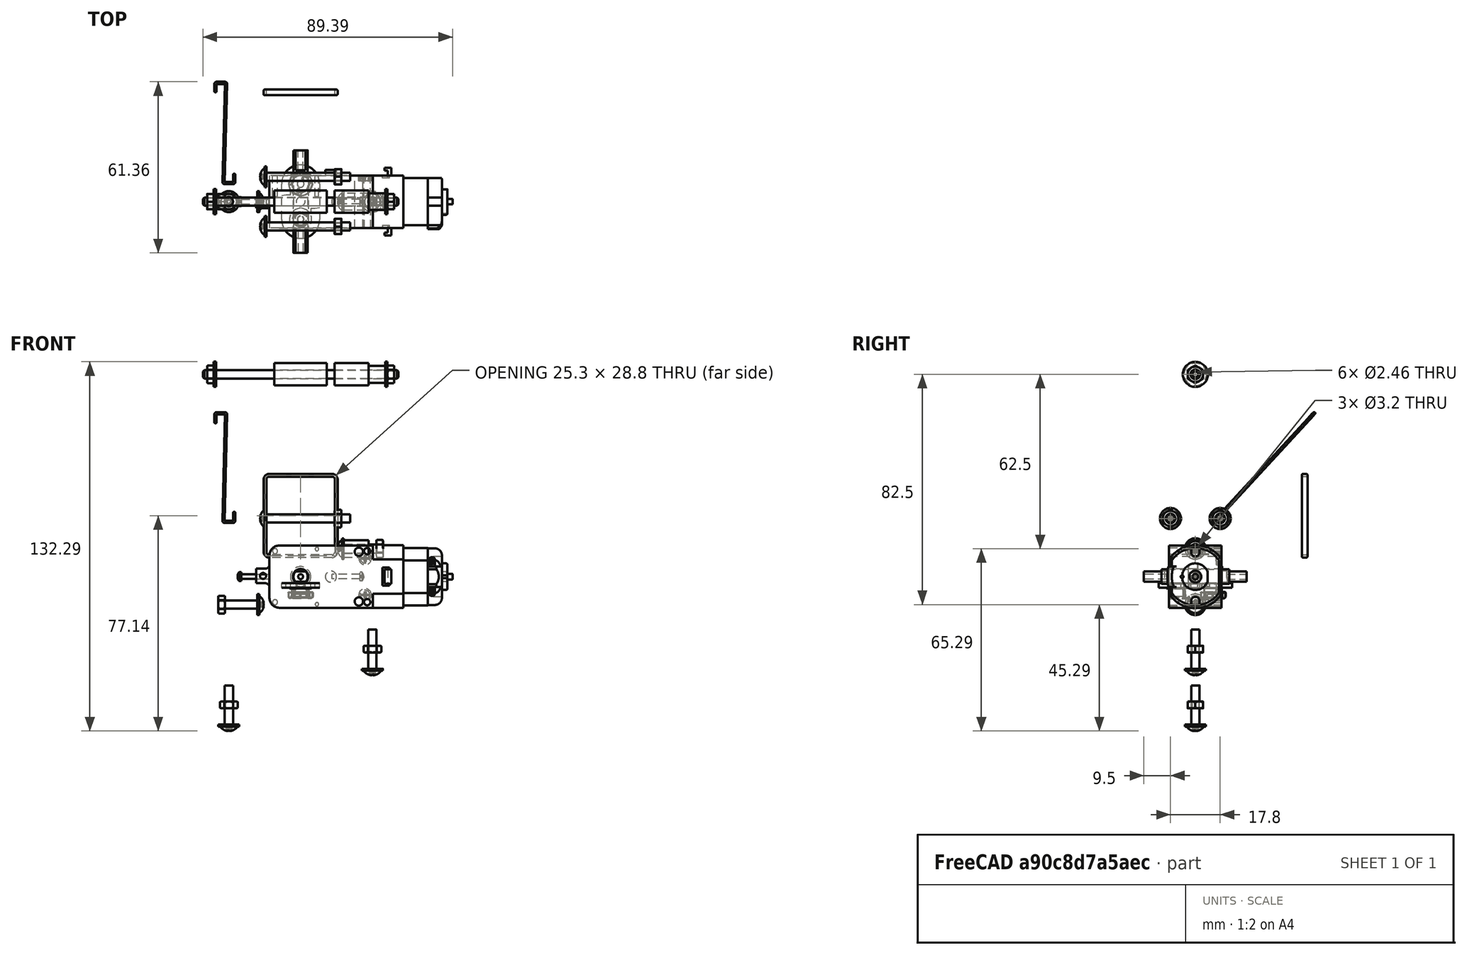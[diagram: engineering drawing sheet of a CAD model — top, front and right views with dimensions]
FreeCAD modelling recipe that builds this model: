
FCSTD DOCUMENT  (FreeCAD 0.21R33771 (Git))
Label: walking_robot_04
License: CERN Open Hardware Licence permissive
LicenseURL: https://cern-ohl.web.cern.ch/
objects: PartDesign::Body×27, PartDesign::SubShapeBinder×26, Sketcher::SketchObject×19, Part::FeaturePython×19, Part::Part2DObjectPython×19, PartDesign::Pad×15, PartDesign::FeatureBase×12, Part::Feature×10, PartDesign::Plane×7, App::DocumentObjectGroup×5, TechDraw::DrawViewDimension×5, PartDesign::FeaturePython×4, PartDesign::Fillet×3, Spreadsheet::Sheet×2, PartDesign::CoordinateSystem×2, Part::Box×2, Part::Cut×2, App::Part×2, PartDesign::AdditivePipe×1, TechDraw::DrawSVGTemplate×1, +4 more types
note: 194 computed .brp shape members not serialized (recipe doc carries the construction recipe); baked Part::Feature solids carry a one-line shape summary decoded from their .brp

FEATURE [Spreadsheet::Sheet] Spreadsheet
  cells = A1='acrylic_thick; B1(acrylic_thick)==4.9 mm; A2='acrylic_thin; B2(acrylic_thin)=2.8; A3='cam_length; B3(cam_length)=10; A4='angle; B4(angle)=270
FEATURE [Part::Feature] Compound002  label="motoreducteur001"
  Placement = pos=(25.85,-9.4,11.15) rot=(-1,0,0;1.5708rad)
  shape: bbox 70.34 x 38.2 x 22.5 mm, 234 faces, 3 solids (baked)
FEATURE [PartDesign::CoordinateSystem] Local_CS002
  AttacherType = Attacher::AttachEngine3D
  AttachmentOffset = pos=(0,0,0) rot=(0,-1,0;1.5708rad)
  MapMode = 11
  Placement = pos=(-2.8e-15,-19.1,1.8e-15) rot=(0,0,-1;1.5708rad)
  Support = -> [Compound002]
FEATURE [PartDesign::CoordinateSystem] Local_CS003
  AttacherType = Attacher::AttachEngine3D
  AttachmentOffset = pos=(0,0,0) rot=(0,1,0;1.5708rad)
  MapMode = 11
  Placement = pos=(-2.8e-15,19.1,1.9e-15) rot=(0,0,1;4.71239rad)
  Support = -> [Compound002]
FEATURE [PartDesign::SubShapeBinder] Binder
  BindCopyOnChange = 0
  BindMode = 0
  ClaimChildren = false
  Context = -> Body [Binder.]
  Fuse = false
  MakeFace = true
  OffsetFill = false
  OffsetIntersection = false
  OffsetJoinType = 0
  OffsetOpenResult = false
  PartialLoad = false
  Relative = true
  Support = -> [Part001]
  _Version = 2
FEATURE [Sketcher::SketchObject] Sketch
  ExternalGeometry = -> [Binder]
  FullyConstrained = true
  MapMode = 5
  Placement = pos=(-18.4,0,0) rot=(0.57735,-0.57735,-0.57735;2.0944rad)
  Support = -> [Binder]
  expr: Constraints[38] = Spreadsheet.cam_length
  expr: Constraints[81] = Spreadsheet.angle
  sketch-geometry (37):
    g0: ArcOfCircle CenterX=3.55 CenterY=5 CenterZ=0 NormalX=0 NormalY=0 NormalZ=1 AngleXU=0 Radius=0.4 StartAngle=0 EndAngle=3.14159
    g1: ArcOfCircle CenterX=3.55 CenterY=-5 CenterZ=0 NormalX=0 NormalY=0 NormalZ=1 AngleXU=0 Radius=0.4 StartAngle=3.14159 EndAngle=6.28319
    g2: LineSegment StartX=3.15 StartY=5 StartZ=0 EndX=3.15 EndY=-5 EndZ=0
    g3: LineSegment StartX=3.95 StartY=-5 StartZ=0 EndX=3.95 EndY=5 EndZ=0
    g4: ArcOfCircle CenterX=-3.55 CenterY=5 CenterZ=0 NormalX=0 NormalY=0 NormalZ=1 AngleXU=0 Radius=0.4 StartAngle=3e-16 EndAngle=3.14159
    g5: ArcOfCircle CenterX=-3.55 CenterY=-5 CenterZ=0 NormalX=0 NormalY=0 NormalZ=1 AngleXU=0 Radius=0.4 StartAngle=3.14159 EndAngle=6.28319
    g6: LineSegment StartX=-3.15 StartY=-5 StartZ=0 EndX=-3.15 EndY=5 EndZ=0
    g7: LineSegment StartX=3.55 StartY=5 StartZ=0 EndX=3.55 EndY=-5 EndZ=0
    g8: LineSegment StartX=-3.55 StartY=5 StartZ=0 EndX=-3.55 EndY=-5 EndZ=0
    g9: ArcOfCircle CenterX=1.55 CenterY=5 CenterZ=0 NormalX=0 NormalY=0 NormalZ=1 AngleXU=0 Radius=0.2 StartAngle=0 EndAngle=3.14159
    g10: ArcOfCircle CenterX=1.55 CenterY=-5 CenterZ=0 NormalX=0 NormalY=0 NormalZ=1 AngleXU=0 Radius=0.2 StartAngle=3.14159 EndAngle=6.28319
    g11: LineSegment StartX=1.35 StartY=5 StartZ=0 EndX=1.35 EndY=2.16333 EndZ=0
    g12: LineSegment StartX=1.75 StartY=-5 StartZ=0 EndX=1.75 EndY=5 EndZ=0
    g13: ArcOfCircle CenterX=-1.55 CenterY=5 CenterZ=0 NormalX=0 NormalY=0 NormalZ=1 AngleXU=0 Radius=0.2 StartAngle=5e-16 EndAngle=3.14159
    g14: ArcOfCircle CenterX=-1.55 CenterY=-5 CenterZ=0 NormalX=0 NormalY=0 NormalZ=1 AngleXU=0 Radius=0.2 StartAngle=3.14159 EndAngle=6.28319
    g15: LineSegment StartX=-1.75 StartY=5 StartZ=0 EndX=-1.75 EndY=-5 EndZ=0
    g16: LineSegment StartX=-1.35 StartY=-5 StartZ=0 EndX=-1.35 EndY=-2.16333 EndZ=0
    g17: LineSegment StartX=1.55 StartY=5 StartZ=0 EndX=1.55 EndY=-5 EndZ=0
    g18: LineSegment StartX=-1.55 StartY=5 StartZ=0 EndX=-1.55 EndY=-5 EndZ=0
    g19: LineSegment StartX=3.55 StartY=-4.2e-15 StartZ=0 EndX=1.55 EndY=-3.8e-15 EndZ=0
    g20: ArcOfCircle CenterX=9.6e-15 CenterY=5 CenterZ=0 NormalX=0 NormalY=0 NormalZ=1 AngleXU=0 Radius=7.5 StartAngle=0 EndAngle=3.14159
    g21: ArcOfCircle CenterX=6.9e-15 CenterY=-10 CenterZ=0 NormalX=0 NormalY=0 NormalZ=1 AngleXU=0 Radius=7.5 StartAngle=3.14159 EndAngle=6.28319
    g22: LineSegment StartX=-7.5 StartY=5 StartZ=0 EndX=-7.5 EndY=-10 EndZ=0
    g23: LineSegment StartX=7.5 StartY=-10 StartZ=0 EndX=7.5 EndY=5 EndZ=0
    g24: LineSegment StartX=8.7e-15 StartY=-3.6e-15 StartZ=0 EndX=9.6e-15 EndY=5 EndZ=0
    g25: LineSegment StartX=8.7e-15 StartY=-3.6e-15 StartZ=0 EndX=6.9e-15 EndY=-10 EndZ=0
    g26: Circle CenterX=6.9e-15 CenterY=-10 CenterZ=0 NormalX=0 NormalY=0 NormalZ=1 AngleXU=0 Radius=3.1
    g27: LineSegment StartX=-3.95 StartY=-5 StartZ=0 EndX=-3.95 EndY=5 EndZ=0
    g28: LineSegment StartX=1.55 StartY=-3.8e-15 StartZ=0 EndX=8.7e-15 EndY=-3.6e-15 EndZ=0
    g29: Circle CenterX=8.7e-15 CenterY=-3.6e-15 CenterZ=0 NormalX=0 NormalY=0 NormalZ=1 AngleXU=0 Radius=1.75
    g30: LineSegment StartX=-1.75 StartY=-4.1e-15 StartZ=0 EndX=-1.85 EndY=-4.1e-15 EndZ=0
    g31: LineSegment StartX=-3.55 StartY=-2.9e-15 StartZ=0 EndX=-1.55 EndY=-3.3e-15 EndZ=0
    g32: LineSegment StartX=8.7e-15 StartY=-3.6e-15 StartZ=0 EndX=-1.55 EndY=-3.3e-15 EndZ=0
    g33: LineSegment StartX=-1.35 StartY=2.16333 StartZ=0 EndX=-1.35 EndY=5 EndZ=0
    g34: LineSegment StartX=1.35 StartY=-2.16333 StartZ=0 EndX=1.35 EndY=-5 EndZ=0
    g35: ArcOfCircle CenterX=8.7e-15 CenterY=-3.6e-15 CenterZ=0 NormalX=0 NormalY=0 NormalZ=1 AngleXU=0 Radius=2.55 StartAngle=1.01289 EndAngle=2.1287
    g36: ArcOfCircle CenterX=8.7e-15 CenterY=-3.6e-15 CenterZ=0 NormalX=0 NormalY=0 NormalZ=1 AngleXU=0 Radius=2.55 StartAngle=4.15448 EndAngle=5.2703
  constraints (89):
    c: Tangent(g0,g2) = -1.5708
    c: Tangent(g2,g1) = -1.5708
    c: Tangent(g1,g3) = -1.5708
    c: Tangent(g5,g6) = -1.5708
    c: Tangent(g6,g4) = -1.5708
    c: Radius(g0) = 0.4
    c: Coincident(g7,g0)
    c: Coincident(g7,g1)
    c: Coincident(g8,g4)
    c: Coincident(g8,g5)
    c: Equal(g7,g8)
    c: Distance(g7) = 10
    c: Tangent(g9,g11) = -1.5708
    c: Tangent(g10,g12) = -1.5708
    c: Tangent(g12,g9) = -1.5708
    c: Tangent(g13,g15) = -1.5708
    c: Tangent(g15,g14) = -1.5708
    c: Tangent(g14,g16) = -1.5708
    c: Coincident(g17,g9)
    c: Coincident(g17,g10)
    c: Coincident(g18,g13)
    c: Coincident(g18,g14)
    c: Equal(g17,g7)
    c: Equal(g8,g18)
    c: Symmetric(g10,g9,g19)
    c: Distance(g19) = 2
    c: Perpendicular(g7,g19)
    c: Parallel(g17,g7)
    c: Parallel(g18,g8)
    c: Tangent(g20,g22) = -1.5708
    c: Tangent(g22,g21) = -1.5708
    c: Tangent(g21,g23) = -1.5708
    c: Tangent(g23,g20) = -1.5708
    c: Equal(g20,g21)
    c: Coincident(g24,g20)
    c: Coincident(g25,g21)
    c: Diameter(g20) = 15
    c: Distance(g24) = 5
    c: Distance(g25) = 10
    c: Coincident(g26,g21)
    c: Diameter(g26) = 6.2
    c: Tangent(g27,g4) = 1.5708
    c: Tangent(g27,g5) = 1.5708
    c: Symmetric(g0,g1,g19)
    c: Coincident(g28,g19)
    c: Parallel(g28,g19)
    c: Perpendicular(g28,g24)
    c: Tangent(g0,g3) = -1.5708
    c: PointOnObject(g30,g29)
    c: Horizontal(g30)
    c: Symmetric(g-5,g-5,g30)
    c: DistanceX(g30,g30) = 0.1
    c: Perpendicular(g25,g28)
    c: Symmetric(g14,g13,g31)
    c: Symmetric(g5,g4,g31)
    c: Equal(g31,g19)
    c: Coincident(g32,g31)
    c: Equal(g28,g32)
    c: Perpendicular(g32,g24)
    c: Perpendicular(g32,g18)
    c: Perpendicular(g18,g31)
    c: Tangent(g15,g29)
    c: PointOnObject(g34,g11)
    c: PointOnObject(g33,g-3)
    c: Parallel(g33,g17)
    c: Parallel(g17,g34)
    c: Tangent(g33,g13) = -1.5708
    c: Tangent(g34,g10) = -1.5708
    c: Coincident(g25,g32)
    c: Coincident(g25,g24)
    c: Coincident(g25,g28)
    c: Coincident(g24,g29)
    c: Coincident(g35,g24)
    c: Coincident(g35,g33)
    c: Coincident(g35,g11)
    c: Coincident(g36,g35)
    c: Coincident(g36,g34)
    c: Equal(g36,g-4)
    c: Coincident(g16,g36)
    c: Parallel(g16,g18)
    c: Coincident(g35,g-4)
    c: Angle(g25) = 4.71239
    c: Equal(g5,g1)
    c: Equal(g1,g4)
    c: Equal(g4,g0)
    c: Equal(g13,g9)
    c: Equal(g9,g14)
    c: Equal(g14,g10)
    c: Radius(g9) = 0.2
FEATURE [PartDesign::SubShapeBinder] Binder001
  BindCopyOnChange = 0
  BindMode = 0
  ClaimChildren = false
  Context = -> Body002 [Binder001.]
  Fuse = false
  MakeFace = true
  OffsetFill = false
  OffsetIntersection = false
  OffsetJoinType = 0
  OffsetOpenResult = false
  PartialLoad = false
  Relative = true
  Support = -> [Part001]
  _Version = 2
FEATURE [Part::Box] Box  label="Cube"
  AttacherType = Attacher::AttachEngine3D
  Height = 10
  Length = 10
  Placement = pos=(-5,18.4,-5) rot=(0,0,1;0rad)
  Width = 10
FEATURE [Part::Box] Box001  label="Cube001"
  AttacherType = Attacher::AttachEngine3D
  Height = 10
  Length = 10
  Placement = pos=(-5,-28.4,-5) rot=(0,0,1;0rad)
  Width = 10
FEATURE [Part::Cut] Cut
  Base = -> Compound002
  Tool = -> Box
FEATURE [Part::Cut] Cut001
  Base = -> Cut
  Tool = -> Box001
FEATURE [App::Part] Part001  label="Motor"
  Group = -> [Box001,Compound002,Local_CS002,Local_CS003,Box,Cut,Cut001]
  Origin = -> Origin004
  Placement = pos=(0,0,0) rot=(-0.57735,0.57735,-0.57735;4.18879rad)
FEATURE [PartDesign::Pad] Pad
  Direction = (-1,2e-16,-2e-16)
  Length = 2.8
  Length2 = 10
  Profile = -> Sketch
  ReferenceAxis = -> Sketch [N_Axis]
  Reversed = true
  Type = 0
  expr: Length = Spreadsheet.acrylic_thin
FEATURE [PartDesign::Body] Body  label="cam_right_1"
  Group = -> [Sketch,Binder,Pad]
  Origin = -> Origin001
  Tip = -> Pad
FEATURE [PartDesign::SubShapeBinder] Binder002
  BindCopyOnChange = 0
  BindMode = 0
  ClaimChildren = false
  Context = -> Body003 [Binder002.]
  Fuse = false
  MakeFace = true
  OffsetFill = false
  OffsetIntersection = false
  OffsetJoinType = 0
  OffsetOpenResult = false
  PartialLoad = false
  Relative = true
  Support = -> [Body]
  _Version = 2
FEATURE [PartDesign::Plane] DatumPlane001
  AttachmentOffset = pos=(0,0,0.1) rot=(0,0,1;0rad)
  Length = 60
  MapMode = 5
  Placement = pos=(-18.5,5.2e-15,-3.9e-15) rot=(-0.57735,0.57735,0.57735;4.18879rad)
  ResizeMode = 0
  Support = -> [Binder002]
  Width = 60
FEATURE [Sketcher::SketchObject] Sketch002
  ExternalGeometry = -> [Binder002]
  FullyConstrained = true
  MapMode = 5
  Placement = pos=(-18.5,5.2e-15,-3.9e-15) rot=(-0.57735,0.57735,0.57735;4.18879rad)
  Support = -> [DatumPlane001]
  sketch-geometry (6):
    g0: ArcOfCircle CenterX=-1.6948e-12 CenterY=5 CenterZ=0 NormalX=0 NormalY=0 NormalZ=1 AngleXU=0 Radius=7.5 StartAngle=2.58e-13 EndAngle=3.14159
    g1: ArcOfCircle CenterX=2.174e-12 CenterY=-10 CenterZ=0 NormalX=0 NormalY=0 NormalZ=1 AngleXU=0 Radius=7.5 StartAngle=3.14159 EndAngle=6.28319
    g2: LineSegment StartX=-7.5 StartY=5 StartZ=0 EndX=-7.5 EndY=-10 EndZ=0
    g3: LineSegment StartX=7.5 StartY=-10 StartZ=0 EndX=7.5 EndY=5 EndZ=0
    g4: Circle CenterX=2.174e-12 CenterY=-10 CenterZ=0 NormalX=0 NormalY=0 NormalZ=1 AngleXU=0 Radius=3.1
    g5: Circle CenterX=0 CenterY=0 CenterZ=0 NormalX=0 NormalY=0 NormalZ=1 AngleXU=0 Radius=1
  constraints (12):
    c: Tangent(g0,g2) = -1.5708
    c: Tangent(g2,g1) = -1.5708
    c: Tangent(g1,g3) = -1.5708
    c: Tangent(g3,g0) = -1.5708
    c: Equal(g0,g1)
    c: Coincident(g0,g-3)
    c: Coincident(g1,g-5)
    c: Equal(g0,g-3)
    c: Coincident(g4,g1)
    c: Equal(g4,g-5)
    c: Coincident(g5,g-6)
    c: Diameter(g5) = 2
FEATURE [PartDesign::Pad] Pad002
  Direction = (-1,2e-16,-2e-16)
  Length = 2.8
  Length2 = 10
  Placement = pos=(-18.5,5e-15,-4e-15) rot=(0.57735,-0.57735,-0.57735;2.0944rad)
  Profile = -> Sketch002
  ReferenceAxis = -> Sketch002 [N_Axis]
  Type = 0
  expr: Length = Spreadsheet.acrylic_thin
FEATURE [PartDesign::Body] Body003  label="cam_right_2"
  Group = -> [Binder002,DatumPlane001,Sketch002,Pad002]
  Origin = -> Origin
  Tip = -> Pad002
FEATURE [PartDesign::SubShapeBinder] Binder003
  BindCopyOnChange = 0
  BindMode = 0
  ClaimChildren = false
  Context = -> Body004 [Binder003.]
  Fuse = false
  MakeFace = true
  OffsetFill = false
  OffsetIntersection = false
  OffsetJoinType = 0
  OffsetOpenResult = false
  PartialLoad = false
  Relative = true
  Support = -> [Body003]
  _Version = 2
FEATURE [PartDesign::Plane] DatumPlane002
  AttachmentOffset = pos=(0,0,0.1) rot=(0,0,1;0rad)
  Length = 60
  MapMode = 5
  Placement = pos=(-21.4,5.3e-15,-1.05e-14) rot=(-0.57735,0.57735,0.57735;4.18879rad)
  ResizeMode = 0
  Support = -> [Binder003]
  Width = 60
FEATURE [Sketcher::SketchObject] Sketch003
  ExternalGeometry = -> [Binder003]
  FullyConstrained = true
  MapMode = 5
  Placement = pos=(-21.4,5.3e-15,-1.05e-14) rot=(-0.57735,0.57735,0.57735;4.18879rad)
  Support = -> [DatumPlane002]
  sketch-geometry (6):
    g0: ArcOfCircle CenterX=-1.6956e-12 CenterY=5 CenterZ=0 NormalX=0 NormalY=0 NormalZ=1 AngleXU=0 Radius=7.5 StartAngle=2.581e-13 EndAngle=3.14159
    g1: ArcOfCircle CenterX=2.1765e-12 CenterY=-10 CenterZ=0 NormalX=0 NormalY=0 NormalZ=1 AngleXU=0 Radius=7.5 StartAngle=3.14159 EndAngle=6.28319
    g2: LineSegment StartX=-7.5 StartY=5 StartZ=0 EndX=-7.5 EndY=-10 EndZ=0
    g3: LineSegment StartX=7.5 StartY=-10 StartZ=0 EndX=7.5 EndY=5 EndZ=0
    g4: Circle CenterX=2.1765e-12 CenterY=-10 CenterZ=0 NormalX=0 NormalY=0 NormalZ=1 AngleXU=0 Radius=3.1
    g5: Circle CenterX=0 CenterY=0 CenterZ=0 NormalX=0 NormalY=0 NormalZ=1 AngleXU=0 Radius=3
  constraints (12):
    c: Tangent(g0,g2) = -1.5708
    c: Tangent(g2,g1) = -1.5708
    c: Tangent(g1,g3) = -1.5708
    c: Tangent(g3,g0) = -1.5708
    c: Equal(g0,g1)
    c: Coincident(g0,g-3)
    c: Coincident(g1,g-5)
    c: Equal(g0,g-3)
    c: Coincident(g4,g1)
    c: Equal(g4,g-5)
    c: Coincident(g5,g-6)
    c: Diameter(g5) = 6
FEATURE [PartDesign::Pad] Pad003
  Direction = (-1,3e-16,-3e-16)
  Length = 2.8
  Length2 = 10
  Placement = pos=(-21.4,5e-15,-1e-14) rot=(0.57735,-0.57735,-0.57735;2.0944rad)
  Profile = -> Sketch003
  ReferenceAxis = -> Sketch003 [N_Axis]
  Type = 0
  expr: Length = Spreadsheet.acrylic_thin
FEATURE [PartDesign::Body] Body004  label="cam_right_3"
  Group = -> [Binder003,DatumPlane002,Sketch003,Pad003]
  Origin = -> Origin005
  Tip = -> Pad003
FEATURE [PartDesign::SubShapeBinder] Binder004
  BindCopyOnChange = 0
  BindMode = 0
  ClaimChildren = false
  Context = -> Body002 [Binder004.]
  Fuse = false
  MakeFace = true
  OffsetFill = false
  OffsetIntersection = false
  OffsetJoinType = 0
  OffsetOpenResult = false
  PartialLoad = false
  Relative = true
  Support = -> [Body004]
  _Version = 2
FEATURE [PartDesign::Plane] DatumPlane003
  AttachmentOffset = pos=(0,0,0.1) rot=(0,0,1;0rad)
  Length = 66.5529
  MapMode = 5
  Placement = pos=(-24.3,8.3e-15,-1.41e-14) rot=(-0.57735,0.57735,0.57735;4.18879rad)
  ResizeMode = 0
  Support = -> [Binder004]
  Width = 153.553
FEATURE [Sketcher::SketchObject] Sketch001
  ExternalGeometry = -> [Binder004]
  FullyConstrained = false
  MapMode = 5
  Placement = pos=(-24.3,8.3e-15,-1.41e-14) rot=(-0.57735,0.57735,0.57735;4.18879rad)
  Support = -> [DatumPlane003]
  expr: Constraints[92] = Spreadsheet.angle
  expr: Constraints[98] = Spreadsheet.acrylic_thin
  sketch-geometry (38):
    g0: LineSegment StartX=-10 StartY=84 StartZ=0 EndX=10 EndY=84 EndZ=0
    g1: LineSegment StartX=10 StartY=84 StartZ=0 EndX=10 EndY=-53 EndZ=0
    g2: LineSegment StartX=10 StartY=-53 StartZ=0 EndX=-10 EndY=-53 EndZ=0
    g3: LineSegment StartX=-10 StartY=-53 StartZ=0 EndX=-10 EndY=84 EndZ=0
    g4: LineSegment StartX=4e-15 StartY=-10 StartZ=0 EndX=-10 EndY=-10 EndZ=0
    g5: LineSegment StartX=4e-15 StartY=-10 StartZ=0 EndX=10 EndY=-10 EndZ=0
    g6: ArcOfCircle CenterX=-2e-16 CenterY=75 CenterZ=0 NormalX=0 NormalY=0 NormalZ=1 AngleXU=0 Radius=3.1 StartAngle=2e-16 EndAngle=3.14159
    g7: ArcOfCircle CenterX=6e-16 CenterY=50 CenterZ=0 NormalX=0 NormalY=0 NormalZ=1 AngleXU=0 Radius=3.1 StartAngle=3.14159 EndAngle=6.28319
    g8: LineSegment StartX=-3.1 StartY=75 StartZ=0 EndX=-3.1 EndY=50 EndZ=0
    g9: LineSegment StartX=3.1 StartY=50 StartZ=0 EndX=3.1 EndY=75 EndZ=0
    g10: LineSegment StartX=-2e-16 StartY=75 StartZ=0 EndX=-4e-16 EndY=84 EndZ=0
    g11: Circle CenterX=4e-15 CenterY=-10 CenterZ=0 NormalX=0 NormalY=0 NormalZ=1 AngleXU=0 Radius=1.55
    g12: LineSegment StartX=0 StartY=0 StartZ=0 EndX=4e-15 EndY=-10 EndZ=0
    g13: Circle CenterX=0 CenterY=71 CenterZ=0 NormalX=0 NormalY=0 NormalZ=1 AngleXU=0 Radius=3.1
    g14: LineSegment StartX=0 StartY=71 StartZ=0 EndX=0 EndY=0 EndZ=0
    g15: LineSegment StartX=6e-16 StartY=50 StartZ=0 EndX=1e-16 EndY=62.5 EndZ=0
    g16: LineSegment StartX=-2e-16 StartY=75 StartZ=0 EndX=1e-16 EndY=62.5 EndZ=0
    g17: LineSegment StartX=-10 StartY=-53 StartZ=0 EndX=-6 EndY=-53 EndZ=0
    g18: LineSegment StartX=-6 StartY=-53 StartZ=0 EndX=-6 EndY=-50.2 EndZ=0
    g19: LineSegment StartX=-6 StartY=-50.2 StartZ=0 EndX=-1.25 EndY=-50.2 EndZ=0
    g20: LineSegment StartX=-1.25 StartY=-50.2 StartZ=0 EndX=-1.25 EndY=-47.2 EndZ=0
    g21: LineSegment StartX=-1.25 StartY=-47.2 StartZ=0 EndX=-2.75 EndY=-47.2 EndZ=0
    g22: LineSegment StartX=-2.75 StartY=-47.2 StartZ=0 EndX=-2.75 EndY=-44.7 EndZ=0
    g23: LineSegment StartX=-2.75 StartY=-44.7 StartZ=0 EndX=-1.25 EndY=-44.7 EndZ=0
    g24: LineSegment StartX=-1.25 StartY=-44.7 StartZ=0 EndX=-1.25 EndY=-37.7 EndZ=0
    g25: LineSegment StartX=-1.25 StartY=-37.7 StartZ=0 EndX=1.25 EndY=-37.7 EndZ=0
    g26: LineSegment StartX=1.25 StartY=-37.7 StartZ=0 EndX=1.25 EndY=-44.7 EndZ=0
    g27: LineSegment StartX=1.25 StartY=-44.7 StartZ=0 EndX=2.75 EndY=-44.7 EndZ=0
    g28: LineSegment StartX=2.75 StartY=-44.7 StartZ=0 EndX=2.75 EndY=-47.2 EndZ=0
    g29: LineSegment StartX=2.75 StartY=-47.2 StartZ=0 EndX=1.25 EndY=-47.2 EndZ=0
    g30: LineSegment StartX=1.25 StartY=-47.2 StartZ=0 EndX=1.25 EndY=-50.2 EndZ=0
    g31: LineSegment StartX=1.25 StartY=-50.2 StartZ=0 EndX=6 EndY=-50.2 EndZ=0
    g32: LineSegment StartX=6 StartY=-50.2 StartZ=0 EndX=6 EndY=-53 EndZ=0
    g33: LineSegment StartX=6 StartY=-53 StartZ=0 EndX=10 EndY=-53 EndZ=0
    g34: LineSegment StartX=-7 StartY=-10 StartZ=0 EndX=-7 EndY=20 EndZ=0
    g35: LineSegment StartX=7 StartY=20 StartZ=0 EndX=7 EndY=-10 EndZ=0
    g36: Circle CenterX=-7 CenterY=20 CenterZ=0 NormalX=0 NormalY=0 NormalZ=1 AngleXU=0 Radius=0.6
    g37: Circle CenterX=7 CenterY=20 CenterZ=0 NormalX=0 NormalY=0 NormalZ=1 AngleXU=0 Radius=0.6
  constraints (105):
    c: Coincident(g0,g1)
    c: Coincident(g1,g2)
    c: Coincident(g2,g3)
    c: Coincident(g3,g0)
    c: Distance(g0) = 20
    c: Perpendicular(g3,g0)
    c: Perpendicular(g1,g2)
    c: Perpendicular(g2,g3)
    c: PointOnObject(g4,g3)
    c: PointOnObject(g5,g1)
    c: Perpendicular(g1,g5)
    c: Perpendicular(g3,g4)
    c: Equal(g4,g5)
    c: Distance(g3) = 137
    c: Tangent(g6,g8) = -1.5708
    c: Tangent(g8,g7) = -1.5708
    c: Tangent(g7,g9) = -1.5708
    c: Tangent(g9,g6) = -1.5708
    c: Equal(g6,g7)
    c: Diameter(g7) = 6.2
    c: Distance(g6,g7) = 25
    c: Coincident(g10,g6)
    c: Perpendicular(g0,g10)
    c: Distance(g10) = 9
    c: Symmetric(g0,g0,g10)
    c: Parallel(g8,g3)
    c: Diameter(g11) = 3.1
    c: Coincident(g14,g13)
    c: DistanceY(g14,g14) = 71
    c: Coincident(g14,g12)
    c: Coincident(g15,g7)
    c: Coincident(g16,g6)
    c: Coincident(g16,g15)
    c: Equal(g16,g15)
    c: Parallel(g16,g8)
    c: Tangent(g13,g9)
    c: Vertical(g14)
    c: Coincident(g17,g3)
    c: Coincident(g17,g18)
    c: Coincident(g18,g19)
    c: Coincident(g19,g20)
    c: Coincident(g20,g21)
    c: Coincident(g21,g22)
    c: Coincident(g22,g23)
    c: Coincident(g23,g24)
    c: Coincident(g24,g25)
    c: Coincident(g25,g26)
    c: Coincident(g26,g27)
    c: Coincident(g27,g28)
    c: Coincident(g28,g29)
    c: Coincident(g29,g30)
    c: Coincident(g30,g31)
    c: Coincident(g31,g32)
    c: Coincident(g32,g33)
    c: Coincident(g33,g1)
    c: Perpendicular(g17,g3)
    c: Perpendicular(g33,g1)
    c: Perpendicular(g32,g33)
    c: Perpendicular(g17,g18)
    c: Perpendicular(g19,g18)
    c: Perpendicular(g32,g31)
    c: Perpendicular(g31,g30)
    c: Perpendicular(g19,g20)
    c: Perpendicular(g29,g30)
    c: Perpendicular(g20,g21)
    c: Perpendicular(g28,g29)
    c: Perpendicular(g22,g21)
    c: Perpendicular(g28,g27)
    c: Perpendicular(g23,g22)
    c: Perpendicular(g27,g26)
    c: Perpendicular(g24,g23)
    c: Equal(g18,g32)
    c: Equal(g30,g20)
    c: Equal(g29,g21)
    c: Equal(g23,g27)
    c: Equal(g19,g31)
    c: Distance(g22,g27) = 5.5
    c: Equal(g25,g22)
    c: Equal(g22,g28)
    c: Distance(g24) = 7
    c: Perpendicular(g25,g26)
    c: Equal(g21,g23)
    c: PointOnObject(g34,g4)
    c: Equal(g34,g35)
    c: Distance(g34,g4) = 3
    c: Coincident(g36,g34)
    c: Coincident(g37,g35)
    c: Equal(g37,g36)
    c: Diameter(g37) = 1.2
    c: Distance(g34) = 30
    c: Perpendicular(g5,g35)
    c: Perpendicular(g4,g34)
    c: Angle(g12) = 4.71239
    c: Equal(g17,g33)
    c: Distance(g17) = 4
    c: DistanceY(g3,g12) = 53
    c: Coincident(g12,g-1)
    c: DistanceY(g22,g22) = 2.5
    c: DistanceY(g18,g18) = 2.8
    c: DistanceY(g20,g20) = 3
    c: Equal(g7,g13)
    c: Coincident(g4,g5)
    c: Coincident(g4,g12)
    c: Coincident(g4,g-3)
    c: Coincident(g4,g11)
FEATURE [PartDesign::Pad] Pad004
  Direction = (-1,5e-16,-5e-16)
  Length = 2.8
  Length2 = 10
  Placement = pos=(-24.3,8e-15,-1.4e-14) rot=(0.57735,-0.57735,-0.57735;2.0944rad)
  Profile = -> Sketch001
  ReferenceAxis = -> Sketch001 [N_Axis]
  Type = 0
  expr: Length = Spreadsheet.acrylic_thin
FEATURE [PartDesign::SubShapeBinder] Binder005
  BindCopyOnChange = 0
  BindMode = 0
  ClaimChildren = false
  Context = -> Body005 [Binder005.]
  Fuse = false
  MakeFace = true
  OffsetFill = false
  OffsetIntersection = false
  OffsetJoinType = 0
  OffsetOpenResult = false
  PartialLoad = false
  Relative = true
  Support = -> [Body004]
  _Version = 2
FEATURE [Part::FeaturePython] Screw  label="M3x14-Screw"  # Fasteners workbench fastener (typed FeaturePython)
  Placement = pos=(-15.5,7.6099e-12,-10) rot=(0,1,0;1.5708rad)
  diameter = 1
  invert = false
  leftHanded = false
  length = 6
  lengthCustom = 14
  matchOuter = false
  offset = 0
  thread = false
  type = 25
FEATURE [Part::FeaturePython] Nut  label="M3-Nut"  # Fasteners workbench fastener (typed FeaturePython)
  Placement = pos=(-29.5,7.6239e-12,-10) rot=(0,1,0;1.5708rad)
  baseObject = -> Screw [Edge71]
  diameter = 4
  invert = false
  leftHanded = false
  matchOuter = false
  offset = 0
  thread = false
  type = 25
FEATURE [PartDesign::SubShapeBinder] Binder008
  BindCopyOnChange = 0
  BindMode = 0
  ClaimChildren = false
  Context = -> Body005 [Binder008.]
  Fuse = false
  MakeFace = true
  OffsetFill = false
  OffsetIntersection = false
  OffsetJoinType = 0
  OffsetOpenResult = false
  PartialLoad = false
  Relative = true
  Support = -> [Body002[Pad004.]]
  _Version = 2
FEATURE [Sketcher::SketchObject] Sketch004
  ExternalGeometry = -> [Binder005]
  FullyConstrained = true
  MapMode = 5
  Placement = pos=(-24.3,-1.36e-14,-3.65e-14) rot=(0.57735,0.57735,0.57735;2.0944rad)
  Support = -> [Binder008]
  sketch-geometry (2):
    g0: Circle CenterX=-2.172e-12 CenterY=-10 CenterZ=0 NormalX=0 NormalY=0 NormalZ=1 AngleXU=0 Radius=3
    g1: Circle CenterX=-2.172e-12 CenterY=-10 CenterZ=0 NormalX=0 NormalY=0 NormalZ=1 AngleXU=0 Radius=1.6
  constraints (4):
    c: Diameter(g1) = 3.2
    c: Diameter(g0) = 6
    c: Coincident(g1,g-3)
    c: Coincident(g0,g1)
FEATURE [PartDesign::Pad] Pad005
  Direction = (1,0,4e-16)
  Length = 8.8
  Length2 = 10
  Profile = -> Sketch004
  ReferenceAxis = -> Sketch004 [N_Axis]
  Type = 0
FEATURE [PartDesign::Body] Body005  label="spacer_right"
  Group = -> [Binder005,Sketch004,Pad005,Binder008]
  Origin = -> Origin006
  Tip = -> Pad005
FEATURE [PartDesign::SubShapeBinder] Binder009
  BindCopyOnChange = 0
  BindMode = 0
  ClaimChildren = false
  Context = -> Body007 [Binder009.]
  Fuse = false
  MakeFace = true
  OffsetFill = false
  OffsetIntersection = false
  OffsetJoinType = 0
  OffsetOpenResult = false
  PartialLoad = false
  Relative = true
  Support = -> [Body002[Pad004.]]
  _Version = 2
FEATURE [PartDesign::Plane] DatumPlane
  Length = 74.3266
  MapMode = 5
  Placement = pos=(5.3e-14,-1.145e-13,-53) rot=(1,0,0;3.14159rad)
  ResizeMode = 0
  Support = -> [Binder009]
  Width = 119.627
FEATURE [Sketcher::SketchObject] Sketch006
  ExternalGeometry = -> [Binder009]
  FullyConstrained = true
  MapMode = 5
  Placement = pos=(5.3e-14,-1.145e-13,-53) rot=(0,0,1;3.14159rad)
  Support = -> [DatumPlane]
  sketch-geometry (51):
    g0: LineSegment StartX=-12.3 StartY=40 StartZ=0 EndX=25.7 EndY=40 EndZ=0
    g1: LineSegment StartX=25.7 StartY=40 StartZ=0 EndX=25.7 EndY=0 EndZ=0
    g2: LineSegment StartX=25.7 StartY=0 StartZ=0 EndX=25.7 EndY=-56 EndZ=0
    g3: LineSegment StartX=25.7 StartY=-56 StartZ=0 EndX=-12.3 EndY=-56 EndZ=0
    g4: ArcOfCircle CenterX=-12.3 CenterY=40 CenterZ=0 NormalX=0 NormalY=0 NormalZ=1 AngleXU=0 Radius=4 StartAngle=1.5708 EndAngle=4.71239
    g5: ArcOfCircle CenterX=-12.3 CenterY=-56 CenterZ=0 NormalX=0 NormalY=0 NormalZ=1 AngleXU=0 Radius=4 StartAngle=1.5708 EndAngle=4.71239
    g6: LineSegment StartX=-12.3 StartY=44 StartZ=0 EndX=25.7 EndY=44 EndZ=0
    g7: LineSegment StartX=-12.3 StartY=36 StartZ=0 EndX=15.7 EndY=36 EndZ=0
    g8: LineSegment StartX=-12.3 StartY=-52 StartZ=0 EndX=15.7 EndY=-52 EndZ=0
    g9: LineSegment StartX=-12.3 StartY=-60 StartZ=0 EndX=25.7 EndY=-60 EndZ=0
    g10: ArcOfCircle CenterX=25.7 CenterY=10.1 CenterZ=0 NormalX=0 NormalY=0 NormalZ=1 AngleXU=0 Radius=8 StartAngle=0 EndAngle=0.895665
    g11: ArcOfCircle CenterX=25.7 CenterY=-9.9 CenterZ=0 NormalX=0 NormalY=0 NormalZ=1 AngleXU=0 Radius=8 StartAngle=3.14159 EndAngle=4.03726
    g12: LineSegment StartX=17.7 StartY=10.1 StartZ=0 EndX=17.7 EndY=-9.9 EndZ=0
    g13: LineSegment StartX=33.7 StartY=-9.9 StartZ=0 EndX=33.7 EndY=10.1 EndZ=0
    g14: LineSegment StartX=20.7 StartY=31 StartZ=0 EndX=20.7 EndY=16.345 EndZ=0
    g15: LineSegment StartX=30.7 StartY=16.345 StartZ=0 EndX=30.7 EndY=39 EndZ=0
    g16: ArcOfCircle CenterX=25.7 CenterY=39 CenterZ=0 NormalX=0 NormalY=0 NormalZ=1 AngleXU=0 Radius=5 StartAngle=0 EndAngle=1.5708
    g17: LineSegment StartX=20.7 StartY=-47 StartZ=0 EndX=20.7 EndY=-16.145 EndZ=0
    g18: LineSegment StartX=30.7 StartY=-16.145 StartZ=0 EndX=30.7 EndY=-55 EndZ=0
    g19: ArcOfCircle CenterX=25.7 CenterY=-55 CenterZ=0 NormalX=0 NormalY=0 NormalZ=1 AngleXU=0 Radius=5 StartAngle=4.71239 EndAngle=6.28319
    g20: ArcOfCircle CenterX=25.7 CenterY=-9.9 CenterZ=0 NormalX=0 NormalY=0 NormalZ=1 AngleXU=0 Radius=8 StartAngle=5.38752 EndAngle=6.28319
    g21: ArcOfCircle CenterX=25.7 CenterY=10.1 CenterZ=0 NormalX=0 NormalY=0 NormalZ=1 AngleXU=0 Radius=8 StartAngle=2.24593 EndAngle=3.14159
    g22: Circle CenterX=25.7 CenterY=0 CenterZ=0 NormalX=0 NormalY=0 NormalZ=1 AngleXU=0 Radius=1.55
    g23: LineSegment StartX=24.2 StartY=10.1 StartZ=0 EndX=27.2 EndY=10.1 EndZ=0
    g24: LineSegment StartX=27.2 StartY=10.1 StartZ=0 EndX=27.2 EndY=6.1 EndZ=0
    g25: LineSegment StartX=27.2 StartY=6.1 StartZ=0 EndX=24.2 EndY=6.1 EndZ=0
    g26: LineSegment StartX=24.2 StartY=6.1 StartZ=0 EndX=24.2 EndY=10.1 EndZ=0
    g27: LineSegment StartX=24.3 StartY=10 StartZ=0 EndX=24.3 EndY=10.1 EndZ=0
    g28: LineSegment StartX=24.3 StartY=10 StartZ=0 EndX=24.2 EndY=10 EndZ=0
    g29: LineSegment StartX=27.1 StartY=6 StartZ=0 EndX=27.2 EndY=6 EndZ=0
    g30: LineSegment StartX=27.1 StartY=6 StartZ=0 EndX=27.1 EndY=6.1 EndZ=0
    g31: LineSegment StartX=24.2 StartY=-5.9 StartZ=0 EndX=27.2 EndY=-5.9 EndZ=0
    g32: LineSegment StartX=27.2 StartY=-5.9 StartZ=0 EndX=27.2 EndY=-9.9 EndZ=0
    g33: LineSegment StartX=27.2 StartY=-9.9 StartZ=0 EndX=24.2 EndY=-9.9 EndZ=0
    g34: LineSegment StartX=24.2 StartY=-9.9 StartZ=0 EndX=24.2 EndY=-5.9 EndZ=0
    g35: LineSegment StartX=24.3 StartY=-6 StartZ=0 EndX=24.3 EndY=-5.9 EndZ=0
    g36: LineSegment StartX=24.3 StartY=-6 StartZ=0 EndX=24.2 EndY=-6 EndZ=0
    g37: LineSegment StartX=27.1 StartY=-10 StartZ=0 EndX=27.2 EndY=-10 EndZ=0
    g38: LineSegment StartX=27.1 StartY=-10 StartZ=0 EndX=27.1 EndY=-9.9 EndZ=0
    g39: ArcOfCircle CenterX=15.7 CenterY=-47 CenterZ=0 NormalX=0 NormalY=0 NormalZ=1 AngleXU=0 Radius=5 StartAngle=4.71239 EndAngle=6.28319
    g40: GeomPoint X=20.7 Y=-52 Z=0
    g41: ArcOfCircle CenterX=15.7 CenterY=31 CenterZ=0 NormalX=0 NormalY=0 NormalZ=1 AngleXU=0 Radius=5 StartAngle=0 EndAngle=1.5708
    g42: GeomPoint X=20.7 Y=36 Z=0
    g43: LineSegment StartX=24.2 StartY=10.1 StartZ=0 EndX=17.7 EndY=10.1 EndZ=0
    g44: LineSegment StartX=27.2 StartY=10.1 StartZ=0 EndX=33.7 EndY=10.1 EndZ=0
    g45: LineSegment StartX=24.2 StartY=-9.9 StartZ=0 EndX=17.7 EndY=-9.9 EndZ=0
    g46: LineSegment StartX=27.2 StartY=-9.9 StartZ=0 EndX=33.7 EndY=-9.9 EndZ=0
    g47: LineSegment StartX=24.3 StartY=1.25 StartZ=0 EndX=24.3 EndY=-1.25 EndZ=0
    g48: LineSegment StartX=27.1 StartY=1.25 StartZ=0 EndX=27.1 EndY=-1.25 EndZ=0
    g49: LineSegment StartX=24.3 StartY=1e-15 StartZ=0 EndX=25.7 EndY=0 EndZ=0
    g50: LineSegment StartX=25.7 StartY=0 StartZ=0 EndX=27.1 EndY=1e-15 EndZ=0
  constraints (133):
    c: Horizontal(g0)
    c: Coincident(g0,g1)
    c: Vertical(g1)
    c: Coincident(g1,g2)
    c: Vertical(g2)
    c: Coincident(g2,g3)
    c: Horizontal(g3)
    c: DistanceY(g2,g2) = 56
    c: Equal(g3,g0)
    c: DistanceX(g0,g0) = 38
    c: Coincident(g4,g0)
    c: Coincident(g5,g3)
    c: Equal(g5,g4)
    c: Diameter(g5) = 8
    c: Horizontal(g6)
    c: Horizontal(g7)
    c: Tangent(g4,g6) = 1.5708
    c: Tangent(g4,g7) = -1.5708
    c: Distance(g42,g1) = 5
    c: Horizontal(g8)
    c: Horizontal(g9)
    c: Tangent(g5,g8) = 1.5708
    c: Tangent(g5,g9) = -1.5708
    c: Equal(g6,g9)
    c: Tangent(g12,g11) = -1.5708
    c: Tangent(g13,g10) = -1.5708
    c: Equal(g10,g11)
    c: Diameter(g10) = 16
    c: Vertical(g14)
    c: PointOnObject(g6,g1)
    c: Vertical(g15)
    c: Tangent(g15,g16) = -1.5708
    c: Tangent(g16,g6) = 1.5708
    c: Distance(g15,g1) = 5
    c: Vertical(g17)
    c: Vertical(g18)
    c: Distance(g18,g2) = 5
    c: Tangent(g19,g9) = -1.5708
    c: Tangent(g19,g18) = 1.5708
    c: Equal(g11,g20)
    c: Coincident(g11,g17)
    c: Coincident(g20,g18)
    c: Coincident(g11,g20)
    c: Tangent(g20,g13) = -1.5708
    c: Equal(g10,g21)
    c: Coincident(g21,g14)
    c: Coincident(g10,g21)
    c: Coincident(g10,g15)
    c: Tangent(g21,g12) = -1.5708
    c: Coincident(g22,g1)
    c: Diameter(g22) = 3.1
    c: Coincident(g23,g24)
    c: Coincident(g24,g25)
    c: Coincident(g25,g26)
    c: Coincident(g26,g23)
    c: Coincident(g28,g27)
    c: Coincident(g30,g29)
    c: Equal(g28,g27)
    c: Equal(g27,g30)
    c: Equal(g30,g29)
    c: Coincident(g31,g32)
    c: Coincident(g32,g33)
    c: Coincident(g33,g34)
    c: Coincident(g34,g31)
    c: Coincident(g36,g35)
    c: Coincident(g38,g37)
    c: Coincident(g37,g-5)
    c: Coincident(g35,g-6)
    c: Coincident(g-4,g29)
    c: Coincident(g27,g-3)
    c: PointOnObject(g40,g8)
    c: PointOnObject(g40,g17)
    c: Tangent(g8,g39) = -1.5708
    c: Tangent(g17,g39) = -1.5708
    c: Radius(g39) = 5
    c: Symmetric(g11,g18,g2)
    c: PointOnObject(g42,g7)
    c: PointOnObject(g42,g14)
    c: Tangent(g7,g41) = 1.5708
    c: Tangent(g14,g41) = 1.5708
    c: Equal(g41,g39)
    c: DistanceY(g1,g1) = 40
    c: Distance(g27) = 0.1
    c: Perpendicular(g-3,g27)
    c: Perpendicular(g28,g27)
    c: PointOnObject(g28,g26)
    c: PointOnObject(g27,g23)
    c: Perpendicular(g28,g26)
    c: Perpendicular(g23,g27)
    c: Perpendicular(g-4,g30)
    c: Perpendicular(g29,g30)
    c: PointOnObject(g29,g24)
    c: PointOnObject(g30,g25)
    c: Perpendicular(g25,g30)
    c: Perpendicular(g29,g24)
    c: Perpendicular(g-5,g38)
    c: Perpendicular(g37,g38)
    c: Perpendicular(g35,g-6)
    c: Perpendicular(g36,g35)
    c: Equal(g35,g36)
    c: Equal(g36,g37)
    c: Equal(g37,g38)
    c: Equal(g38,g27)
    c: PointOnObject(g35,g31)
    c: PointOnObject(g36,g34)
    c: Perpendicular(g34,g36)
    c: Perpendicular(g31,g35)
    c: PointOnObject(g38,g33)
    c: PointOnObject(g37,g32)
    c: Perpendicular(g32,g37)
    c: Perpendicular(g33,g38)
    c: Coincident(g43,g23)
    c: Coincident(g43,g12)
    c: Coincident(g44,g23)
    c: Coincident(g44,g10)
    c: Perpendicular(g44,g24)
    c: Perpendicular(g43,g26)
    c: Coincident(g45,g33)
    c: Coincident(g45,g11)
    c: Coincident(g46,g32)
    c: Coincident(g46,g13)
    c: Perpendicular(g32,g46)
    c: Coincident(g47,g-8)
    c: Coincident(g47,g-7)
    c: Coincident(g48,g-8)
    c: Coincident(g48,g-7)
    c: Coincident(g50,g49)
    c: PointOnObject(g50,g48)
    c: Equal(g49,g50)
    c: Perpendicular(g49,g47)
    c: Perpendicular(g48,g50)
    c: Symmetric(g47,g47,g49)
    c: Coincident(g22,g49)
FEATURE [PartDesign::Pad] Pad006
  Direction = (-6e-16,2.1e-15,1)
  Length = 2.8
  Length2 = 10
  Placement = pos=(2.9e-14,-1.09e-13,-53) rot=(1,0,0;3.14159rad)
  Profile = -> Sketch006
  ReferenceAxis = -> Sketch006 [N_Axis]
  Type = 0
  expr: Length = Spreadsheet.acrylic_thin
FEATURE [PartDesign::Body] Body007  label="feet_right"
  Group = -> [Sketch006,Binder009,DatumPlane,Pad006]
  Origin = -> Origin009
  Tip = -> Pad006
FEATURE [PartDesign::FeatureBase] Clone
  BaseFeature = -> Body
FEATURE [PartDesign::Body] Body008  label="cam_left_1"
  Group = -> [Clone]
  Origin = -> Origin010
  Placement = pos=(0,0,0) rot=(0,1,0;3.14159rad)
  Tip = -> Clone
FEATURE [PartDesign::FeatureBase] Clone001
  BaseFeature = -> Body003
FEATURE [PartDesign::Body] Body009  label="cam_left_2"
  Group = -> [Clone001]
  Origin = -> Origin011
  Placement = pos=(0,0,0) rot=(0,1,0;3.14159rad)
  Tip = -> Clone001
FEATURE [PartDesign::FeatureBase] Clone002
  BaseFeature = -> Body004
FEATURE [PartDesign::Body] Body010  label="cam_left_3"
  Group = -> [Clone002]
  Origin = -> Origin012
  Placement = pos=(0,0,0) rot=(0,1,0;3.14159rad)
  Tip = -> Clone002
FEATURE [PartDesign::FeatureBase] Clone003
  BaseFeature = -> Body005
FEATURE [PartDesign::Body] Body011  label="spacer_left"
  Group = -> [Clone003]
  Origin = -> Origin013
  Placement = pos=(0,0,0) rot=(0,1,0;3.14159rad)
  Tip = -> Clone003
FEATURE [PartDesign::FeatureBase] Clone007
  BaseFeature = -> Body007
FEATURE [PartDesign::Body] Body015  label="feet_left"
  Group = -> [Clone007]
  Origin = -> Origin017
  Placement = pos=(1e-14,0,-83.2) rot=(0,1,0;3.14159rad)
  Tip = -> Clone007
FEATURE [PartDesign::Fillet] Fillet
  Base = -> Pad004 [Edge1,Edge2,Edge11,Edge14,Edge53,Edge20,Edge38,Edge35,Edge50,Edge23,Edge41,Edge32,Edge26,Edge47,Edge44,Edge29]
  BaseFeature = -> Pad004
  Placement = pos=(-24.3,8e-15,-1.4e-14) rot=(0.57735,-0.57735,-0.57735;2.0944rad)
  Radius = 0.4
  SupportTransform = false
  UseAllEdges = false
FEATURE [PartDesign::Fillet] Fillet001
  Base = -> Fillet [Edge91,Edge93]
  BaseFeature = -> Fillet
  Placement = pos=(-24.3,8e-15,-1.4e-14) rot=(0.57735,-0.57735,-0.57735;2.0944rad)
  Radius = 5
  SupportTransform = false
  UseAllEdges = false
FEATURE [PartDesign::SubShapeBinder] Binder010
  BindCopyOnChange = 0
  BindMode = 0
  ClaimChildren = false
  Context = -> Body017 [Binder010.]
  Fuse = false
  MakeFace = true
  OffsetFill = false
  OffsetIntersection = false
  OffsetJoinType = 0
  OffsetOpenResult = false
  PartialLoad = false
  Relative = true
  Support = -> [Part001]
  _Version = 2
FEATURE [PartDesign::SubShapeBinder] Binder011
  BindCopyOnChange = 0
  BindMode = 0
  ClaimChildren = false
  Context = -> Body017 [Binder011.]
  Fuse = false
  MakeFace = true
  OffsetFill = false
  OffsetIntersection = false
  OffsetJoinType = 0
  OffsetOpenResult = false
  PartialLoad = false
  Relative = true
  Support = -> [Body002]
  _Version = 2
FEATURE [PartDesign::SubShapeBinder] Binder012
  BindCopyOnChange = 0
  BindMode = 0
  ClaimChildren = false
  Context = -> Body017 [Binder012.]
  Fuse = false
  MakeFace = true
  OffsetFill = false
  OffsetIntersection = false
  OffsetJoinType = 0
  OffsetOpenResult = false
  PartialLoad = false
  Relative = true
  Support = -> [Body014]
  _Version = 2
FEATURE [Sketcher::SketchObject] Sketch007
  ExternalGeometry = -> [Binder010,Binder011,Binder012]
  FullyConstrained = true
  MapMode = 5
  Placement = pos=(-9.4,0,0) rot=(0.57735,-0.57735,-0.57735;2.0944rad)
  Support = -> [Binder010]
  expr: Constraints[77] = Spreadsheet.acrylic_thin
  expr: Constraints[80] = Spreadsheet.acrylic_thin
  expr: Constraints[84] = Spreadsheet.acrylic_thin * 2
  sketch-geometry (39):
    g0: Circle CenterX=0 CenterY=10.85 CenterZ=0 NormalX=0 NormalY=0 NormalZ=1 AngleXU=0 Radius=2.1
    g1: Circle CenterX=-8.9 CenterY=20.85 CenterZ=0 NormalX=0 NormalY=0 NormalZ=1 AngleXU=0 Radius=1.55
    g2: Circle CenterX=8.9 CenterY=20.85 CenterZ=0 NormalX=0 NormalY=0 NormalZ=1 AngleXU=0 Radius=1.55
    g3: Circle CenterX=-1.19e-14 CenterY=72.5 CenterZ=0 NormalX=0 NormalY=0 NormalZ=1 AngleXU=0 Radius=1.55
    g4: ArcOfCircle CenterX=-8.15 CenterY=75.1 CenterZ=0 NormalX=0 NormalY=0 NormalZ=1 AngleXU=0 Radius=3 StartAngle=1.5708 EndAngle=3.14159
    g5: ArcOfCircle CenterX=8.15 CenterY=75.1 CenterZ=0 NormalX=0 NormalY=0 NormalZ=1 AngleXU=0 Radius=3 StartAngle=1.6841e-12 EndAngle=1.5708
    g6: LineSegment StartX=11.15 StartY=75.1 StartZ=0 EndX=11.15 EndY=36.85 EndZ=0
    g7: ArcOfCircle CenterX=8.15 CenterY=9.85 CenterZ=0 NormalX=0 NormalY=0 NormalZ=1 AngleXU=0 Radius=3 StartAngle=4.71239 EndAngle=6.28319
    g8: LineSegment StartX=8.15 StartY=6.85 StartZ=0 EndX=-11.15 EndY=6.85 EndZ=0
    g9: LineSegment StartX=-11.15 StartY=39.85 StartZ=0 EndX=-11.15 EndY=75.1 EndZ=0
    g10: GeomPoint X=11.15 Y=6.85 Z=0
    g11: ArcOfCircle CenterX=-3.18082 CenterY=49.59 CenterZ=0 NormalX=0 NormalY=0 NormalZ=1 AngleXU=0 Radius=3 StartAngle=1.5708 EndAngle=3.14159
    g12: LineSegment StartX=-3.18082 StartY=52.59 StartZ=0 EndX=3.18082 EndY=52.59 EndZ=0
    g13: ArcOfCircle CenterX=3.18082 CenterY=49.59 CenterZ=0 NormalX=0 NormalY=0 NormalZ=1 AngleXU=0 Radius=3 StartAngle=-7.3053e-12 EndAngle=1.5708
    g14: ArcOfCircle CenterX=3.18082 CenterY=28.85 CenterZ=0 NormalX=0 NormalY=0 NormalZ=1 AngleXU=0 Radius=3 StartAngle=4.71239 EndAngle=6.28319
    g15: LineSegment StartX=3.18082 StartY=25.85 StartZ=0 EndX=-3.18082 EndY=25.85 EndZ=0
    g16: ArcOfCircle CenterX=-3.18082 CenterY=28.85 CenterZ=0 NormalX=0 NormalY=0 NormalZ=1 AngleXU=0 Radius=3 StartAngle=3.14159 EndAngle=4.71239
    g17: LineSegment StartX=-6.18082 StartY=28.85 StartZ=0 EndX=-6.18082 EndY=49.59 EndZ=0
    g18: LineSegment StartX=6.18082 StartY=49.59 StartZ=0 EndX=6.18082 EndY=28.85 EndZ=0
    g19: LineSegment StartX=-11.15 StartY=6.85 StartZ=0 EndX=-37.15 EndY=6.85 EndZ=0
    g20: ArcOfCircle CenterX=-37.15 CenterY=7.85 CenterZ=0 NormalX=0 NormalY=0 NormalZ=1 AngleXU=0 Radius=1 StartAngle=3.14159 EndAngle=4.71239
    g21: ArcOfCircle CenterX=-39.15 CenterY=7.85 CenterZ=0 NormalX=0 NormalY=0 NormalZ=1 AngleXU=0 Radius=1 StartAngle=0 EndAngle=3.14159
    g22: ArcOfCircle CenterX=-41.15 CenterY=7.85 CenterZ=0 NormalX=0 NormalY=0 NormalZ=1 AngleXU=0 Radius=1 StartAngle=3.14159 EndAngle=6.28319
    g23: LineSegment StartX=-42.15 StartY=7.85 StartZ=0 EndX=-42.15 EndY=35.85 EndZ=0
    g24: ArcOfCircle CenterX=-41.15 CenterY=35.85 CenterZ=0 NormalX=0 NormalY=0 NormalZ=1 AngleXU=0 Radius=1 StartAngle=-1.8e-15 EndAngle=3.14159
    g25: ArcOfCircle CenterX=-39.15 CenterY=35.85 CenterZ=0 NormalX=0 NormalY=0 NormalZ=1 AngleXU=0 Radius=1 StartAngle=3.14159 EndAngle=6.28319
    g26: ArcOfCircle CenterX=-37.15 CenterY=35.85 CenterZ=0 NormalX=0 NormalY=0 NormalZ=1 AngleXU=0 Radius=1 StartAngle=1.5708 EndAngle=3.14159
    g27: LineSegment StartX=-37.15 StartY=36.85 StartZ=0 EndX=-14.15 EndY=36.85 EndZ=0
    g28: ArcOfCircle CenterX=-14.15 CenterY=39.85 CenterZ=0 NormalX=0 NormalY=0 NormalZ=1 AngleXU=0 Radius=3 StartAngle=4.71239 EndAngle=6.28319
    g29: LineSegment StartX=-8.15 StartY=78.1 StartZ=0 EndX=8.15 EndY=78.1 EndZ=0
    g30: ArcOfCircle CenterX=12.55 CenterY=13.85 CenterZ=0 NormalX=0 NormalY=0 NormalZ=1 AngleXU=0 Radius=1.4 StartAngle=6e-16 EndAngle=3.14159
    g31: LineSegment StartX=13.95 StartY=13.85 StartZ=0 EndX=13.95 EndY=8.25 EndZ=0
    g32: ArcOfCircle CenterX=15.35 CenterY=8.25 CenterZ=0 NormalX=0 NormalY=0 NormalZ=1 AngleXU=0 Radius=1.4 StartAngle=3.14159 EndAngle=6.28319
    g33: LineSegment StartX=16.75 StartY=8.25 StartZ=0 EndX=16.75 EndY=39.65 EndZ=0
    g34: ArcOfCircle CenterX=15.35 CenterY=39.65 CenterZ=0 NormalX=0 NormalY=0 NormalZ=1 AngleXU=0 Radius=1.4 StartAngle=-9e-16 EndAngle=3.14159
    g35: LineSegment StartX=13.95 StartY=39.65 StartZ=0 EndX=13.95 EndY=36.85 EndZ=0
    g36: LineSegment StartX=13.95 StartY=36.85 StartZ=0 EndX=11.15 EndY=36.85 EndZ=0
    g37: LineSegment StartX=8.15 StartY=6.85 StartZ=0 EndX=15.35 EndY=6.85 EndZ=0
    g38: LineSegment StartX=11.15 StartY=13.85 StartZ=0 EndX=11.15 EndY=9.85 EndZ=0
  constraints (98):
    c: Equal(g1,g2)
    c: Diameter(g1) = 3.1
    c: Diameter(g3) = 3.1
    c: Tangent(g5,g6) = 1.5708
    c: Tangent(g7,g8) = 1.5708
    c: Tangent(g9,g4) = 1.5708
    c: Horizontal(g8)
    c: Vertical(g6)
    c: Vertical(g9)
    c: Equal(g4,g5)
    c: Equal(g5,g7)
    c: PointOnObject(g10,g6)
    c: PointOnObject(g10,g8)
    c: Distance(g0,g8) = 4
    c: Tangent(g11,g12) = 1.5708
    c: Tangent(g12,g13) = 1.5708
    c: Tangent(g14,g15) = 1.5708
    c: Tangent(g15,g16) = 1.5708
    c: Tangent(g17,g11) = 1.5708
    c: Horizontal(g12)
    c: Horizontal(g15)
    c: Vertical(g17)
    c: Radius(g11) = 3
    c: Coincident(g0,g-5)
    c: Coincident(g1,g-3)
    c: Coincident(g2,g-4)
    c: PointOnObject(g38,g-7)
    c: Tangent(g16,g17) = 1.5708
    c: Vertical(g18)
    c: Tangent(g18,g14) = 1.5708
    c: Tangent(g18,g13) = 1.5708
    c: Equal(g11,g13)
    c: Equal(g13,g14)
    c: Equal(g14,g16)
    c: PointOnObject(g16,g-10)
    c: PointOnObject(g14,g-11)
    c: Horizontal(g15,g-10)
    c: PointOnObject(g19,g-6)
    c: Horizontal(g19)
    c: Tangent(g19,g20) = 1.5708
    c: Tangent(g20,g21) = 1.5708
    c: Tangent(g21,g22) = 1.5708
    c: Vertical(g23)
    c: Tangent(g23,g24) = 1.5708
    c: Tangent(g24,g25) = 1.5708
    c: Tangent(g25,g26) = 1.5708
    c: Horizontal(g27)
    c: Coincident(g8,g19)
    c: Tangent(g9,g28) = -1.5708
    c: Tangent(g27,g28) = -1.5708
    c: Tangent(g26,g27) = 1.5708
    c: Tangent(g22,g23) = 1.5708
    c: Equal(g20,g21)
    c: Equal(g20,g22)
    c: Equal(g20,g24)
    c: Equal(g20,g25)
    c: Equal(g20,g26)
    c: Radius(g20) = 1
    c: Angle(g20) = 1.5708
    c: Angle(g21) = 3.14159
    c: Angle(g26) = 1.5708
    c: Angle(g25) = 3.14159
    c: Radius(g4) = 3
    c: Equal(g28,g4)
    c: DistanceY(g8,g27) = 30
    c: DistanceX(g19,g19) = 26
    c: Vertical(g9,g8)
    c: Horizontal(g29)
    c: Tangent(g29,g4) = 1.5708
    c: Tangent(g29,g5) = 1.5708
    c: Vertical(g31)
    c: Tangent(g31,g32) = -1.5708
    c: Vertical(g33)
    c: Vertical(g35)
    c: Coincident(g35,g36)
    c: Horizontal(g36)
    c: Equal(g36,g35)
    c: DistanceX(g36,g36) = 2.8
    c: Tangent(g33,g34) = -1.5708
    c: Tangent(g34,g35) = -1.5708
    c: Diameter(g34) = 2.8
    c: Equal(g32,g34)
    c: Tangent(g32,g33) = -1.5708
    c: Tangent(g30,g31) = 1.5708
    c: DistanceY(g32,g30) = 5.6
    c: Tangent(g30,g6) = -1.5708
    c: Coincident(g37,g7)
    c: Horizontal(g37)
    c: Horizontal(g36,g27)
    c: Tangent(g37,g32) = -1.5708
    c: Coincident(g6,g36)
    c: Vertical(g38)
    c: Coincident(g38,g30)
    c: Tangent(g38,g7) = 1.5708
    c: Diameter(g0) = 4.2
    c: Symmetric(g-12,g-13,g3)
    c: Tangent(g29,g-12)
    c: PointOnObject(g11,g-14)
FEATURE [PartDesign::Pad] Pad007
  Direction = (-1,0,0)
  Length = 2.8
  Length2 = 10
  Profile = -> Sketch007
  ReferenceAxis = -> Sketch007 [N_Axis]
  Type = 0
  expr: Length = Spreadsheet.acrylic_thin
FEATURE [PartDesign::Body] Body017  label="body_right"
  Group = -> [Sketch007,Binder010,Binder011,Binder012,Pad007]
  Origin = -> Origin019
  Tip = -> Pad007
FEATURE [Part::Feature] Part__Feature  label="batt_9V005_cp_sp"
  shape: bbox 13.59 x 26.29 x 1.575 mm, 21 faces (baked)
FEATURE [Part::Feature] Part__Feature003  label="batt_9V005_cp_sp003"
  shape: bbox 7.925 x 7.925 x 3.557 mm, 27 faces (baked)
FEATURE [Part::Feature] Part__Feature004  label="batt_9V005_cp_sp004"
  shape: bbox 9.35 x 9.35 x 4.186 mm, 125 faces (baked)
FEATURE [Part::Feature] Part__Feature005  label="batt_9V005_cp_sp005"
  shape: bbox 15.74 x 25.33 x 0.8457 mm, 1 faces, 0 solids (baked)
FEATURE [Part::Feature] Part__Feature006  label="batt_9V005_cp_sp006"
  shape: bbox 15.38 x 24.78 x 2e-07 mm, 1 faces, 0 solids (baked)
FEATURE [Part::Feature] Part__Feature007  label="batt_9V005_cp_sp007"
  shape: bbox 16.6 x 26 x 42.82 mm, 188 faces, 0 solids (baked)
FEATURE [Part::Feature] Part__Feature008  label="batt_9V005_cp_sp008"
  shape: bbox 7.6 x 8.776 x 3 mm, 28 faces, 0 solids (baked)
FEATURE [Part::Feature] Part__Feature009  label="batt_9V005_cp_sp009"
  shape: bbox 6.35 x 6.35 x 1.5 mm, 2 faces, 0 solids (baked)
FEATURE [Part::Feature] Part__Feature010  label="batt_9V005_cp_sp010"
  shape: bbox 8 x 8 x 3.2 mm, 10 faces, 0 solids (baked)
FEATURE [App::Part] batt_9V005_cp_sp  label="batt_9V005_cp_sp011"
  Group = -> [Part__Feature,Part__Feature003,Part__Feature004,Part__Feature005,Part__Feature006,Part__Feature007,Part__Feature008,Part__Feature009,Part__Feature010]
  Origin = -> Origin020
  Placement = pos=(0,25,40) rot=(0,0,1;0rad)
FEATURE [PartDesign::FeatureBase] Clone008
  BaseFeature = -> Body017
FEATURE [PartDesign::Body] Body018  label="body_left"
  Group = -> [Clone008]
  Origin = -> Origin021
  Placement = pos=(21.6,0,0) rot=(0,0,1;0rad)
  Tip = -> Clone008
FEATURE [PartDesign::SubShapeBinder] Binder013
  BindCopyOnChange = 0
  BindMode = 0
  ClaimChildren = false
  Context = -> Body019 [Binder013.]
  Fuse = false
  MakeFace = true
  OffsetFill = false
  OffsetIntersection = false
  OffsetJoinType = 0
  OffsetOpenResult = false
  PartialLoad = false
  Relative = true
  Support = -> [Body017]
  _Version = 2
FEATURE [PartDesign::SubShapeBinder] Binder014
  BindCopyOnChange = 0
  BindMode = 0
  ClaimChildren = false
  Context = -> Body019 [Binder014.]
  Fuse = false
  MakeFace = true
  OffsetFill = false
  OffsetIntersection = false
  OffsetJoinType = 0
  OffsetOpenResult = false
  PartialLoad = false
  Relative = true
  Support = -> [Body018]
  _Version = 2
FEATURE [Sketcher::SketchObject] Sketch008
  ExternalGeometry = -> [Binder014]
  FullyConstrained = true
  MapMode = 5
  Placement = pos=(0,0,0) rot=(0.57735,0.57735,0.57735;2.0944rad)
  Support = -> [YZ_Plane020]
  sketch-geometry (2):
    g0: Circle CenterX=5e-16 CenterY=72.5 CenterZ=0 NormalX=0 NormalY=0 NormalZ=1 AngleXU=0 Radius=1.55
    g1: Circle CenterX=5e-16 CenterY=72.5 CenterZ=0 NormalX=0 NormalY=0 NormalZ=1 AngleXU=0 Radius=4
  constraints (4):
    c: Coincident(g0,g-3)
    c: Coincident(g1,g0)
    c: Equal(g0,g-3)
    c: Diameter(g1) = 8
FEATURE [PartDesign::Pad] Pad008
  Direction = (1,-2e-16,3e-16)
  Length = 18.8
  Length2 = 10
  Midplane = true
  Placement = pos=(0,0,0) rot=(0.57735,0.57735,0.57735;2.0944rad)
  Profile = -> Sketch008
  ReferenceAxis = -> Sketch008 [N_Axis]
  Type = 0
FEATURE [PartDesign::Body] Body019  label="spacer_top_centre"
  Group = -> [Sketch008,Binder013,Binder014,Pad008]
  Origin = -> Origin022
  Tip = -> Pad008
FEATURE [PartDesign::SubShapeBinder] Binder015
  BindCopyOnChange = 0
  BindMode = 0
  ClaimChildren = false
  Context = -> Body020 [Binder015.]
  Fuse = false
  MakeFace = true
  OffsetFill = false
  OffsetIntersection = false
  OffsetJoinType = 0
  OffsetOpenResult = false
  PartialLoad = false
  Relative = true
  Support = -> [Body017]
  _Version = 2
FEATURE [PartDesign::SubShapeBinder] Binder016
  BindCopyOnChange = 0
  BindMode = 0
  ClaimChildren = false
  Context = -> Body020 [Binder016.]
  Fuse = false
  MakeFace = true
  OffsetFill = false
  OffsetIntersection = false
  OffsetJoinType = 0
  OffsetOpenResult = false
  PartialLoad = false
  Relative = true
  Support = -> [Body002]
  _Version = 2
FEATURE [Sketcher::SketchObject] Sketch009
  ExternalGeometry = -> [Binder015]
  FullyConstrained = true
  MapMode = 5
  Placement = pos=(-12.2,0,0) rot=(0.57735,-0.57735,-0.57735;2.0944rad)
  Support = -> [Binder015]
  sketch-geometry (2):
    g0: Circle CenterX=-5.8e-15 CenterY=72.5 CenterZ=0 NormalX=0 NormalY=0 NormalZ=1 AngleXU=0 Radius=1.55
    g1: Circle CenterX=-5.8e-15 CenterY=72.5 CenterZ=0 NormalX=0 NormalY=0 NormalZ=1 AngleXU=0 Radius=4
  constraints (4):
    c: Coincident(g1,g0)
    c: Diameter(g1) = 8
    c: Equal(g0,g-3)
    c: Coincident(g0,g-3)
FEATURE [PartDesign::Pad] Pad009
  Direction = (-1,0,0)
  Length = 10
  Length2 = 10
  Profile = -> Sketch009
  ReferenceAxis = -> Sketch009 [N_Axis]
  Type = 3
  UpToFace = -> Binder016 [Face1]
FEATURE [Sketcher::SketchObject] Sketch010
  ExternalGeometry = -> [Pad009,Binder016]
  FullyConstrained = true
  MapMode = 5
  Placement = pos=(-24.3,-1.09e-14,-2.58e-14) rot=(0.57735,-0.57735,-0.57735;2.0944rad)
  Support = -> [Pad009]
  sketch-geometry (2):
    g0: Circle CenterX=-2.06e-14 CenterY=72.5 CenterZ=0 NormalX=0 NormalY=0 NormalZ=1 AngleXU=0 Radius=3
    g1: Circle CenterX=-2.06e-14 CenterY=72.5 CenterZ=0 NormalX=0 NormalY=0 NormalZ=1 AngleXU=0 Radius=1.55
  constraints (4):
    c: Equal(g1,g-6)
    c: Coincident(g0,g-6)
    c: Coincident(g0,g1)
    c: Diameter(g0) = 6
FEATURE [PartDesign::Pad] Pad010
  BaseFeature = -> Pad009
  Direction = (-1,-3e-16,-1e-15)
  Length = 6
  Length2 = 10
  Profile = -> Sketch010
  ReferenceAxis = -> Sketch010 [N_Axis]
  Type = 0
  expr: Length = Spreadsheet.acrylic_thin * 2 + 0.4
FEATURE [PartDesign::Body] Body020  label="spacer_top_right"
  Group = -> [Binder015,Binder016,Sketch009,Pad009,Sketch010,Pad010]
  Origin = -> Origin023
  Tip = -> Pad010
FEATURE [PartDesign::FeatureBase] Clone009
  BaseFeature = -> Body020
FEATURE [PartDesign::Body] Body021  label="spacer_top_left"
  Group = -> [Clone009]
  Origin = -> Origin024
  Placement = pos=(0,0,0) rot=(0,0,1;3.14159rad)
  Tip = -> Clone009
FEATURE [Part::FeaturePython] ThreadedRod  label="M3x70-ThreadedRod"  # Fasteners workbench fastener (typed FeaturePython)
  Placement = pos=(-35,0,72.5) rot=(0,-1,0;1.5708rad)
  diameter = 4
  diameterCustom = 6
  invert = false
  leftHanded = false
  length = 70
  matchOuter = false
  offset = 0
  pitchCustom = 1
  thread = false
  type = 4
FEATURE [PartDesign::SubShapeBinder] Binder017
  BindCopyOnChange = 0
  BindMode = 0
  ClaimChildren = false
  Context = -> Body022 [Binder017.]
  Fuse = false
  MakeFace = true
  OffsetFill = false
  OffsetIntersection = false
  OffsetJoinType = 0
  OffsetOpenResult = false
  PartialLoad = false
  Relative = true
  Support = -> [Body017]
  _Version = 2
FEATURE [PartDesign::SubShapeBinder] Binder018
  BindCopyOnChange = 0
  BindMode = 0
  ClaimChildren = false
  Context = -> Body022 [Binder018.]
  Fuse = false
  MakeFace = true
  OffsetFill = false
  OffsetIntersection = false
  OffsetJoinType = 0
  OffsetOpenResult = false
  PartialLoad = false
  Relative = true
  Support = -> [Body018]
  _Version = 2
FEATURE [PartDesign::SubShapeBinder] Binder019
  BindCopyOnChange = 0
  BindMode = 0
  ClaimChildren = false
  Context = -> Body022 [Binder019.]
  Fuse = false
  MakeFace = true
  OffsetFill = false
  OffsetIntersection = false
  OffsetJoinType = 0
  OffsetOpenResult = false
  PartialLoad = false
  Relative = true
  Support = -> [Part001]
  _Version = 2
FEATURE [Sketcher::SketchObject] Sketch011
  ExternalGeometry = -> [Binder017,Binder018]
  FullyConstrained = true
  MapMode = 5
  Placement = pos=(0,-11.15,0) rot=(1,0,0;1.5708rad)
  Support = -> [Binder019]
  expr: Constraints[24] = Spreadsheet.acrylic_thin - 0.3
  expr: Constraints[25] = Spreadsheet.acrylic_thin + 0.3
  sketch-geometry (21):
    g0: LineSegment StartX=-9.4 StartY=36.85 StartZ=0 EndX=-12.2 EndY=36.85 EndZ=0
    g1: LineSegment StartX=-12.2 StartY=36.85 StartZ=0 EndX=-12.2 EndY=76.6 EndZ=0
    g2: ArcOfCircle CenterX=-10.7 CenterY=76.6 CenterZ=0 NormalX=0 NormalY=0 NormalZ=1 AngleXU=0 Radius=1.5 StartAngle=1.5708 EndAngle=3.14159
    g3: LineSegment StartX=-5 StartY=79.6 StartZ=0 EndX=-5 EndY=83.1 EndZ=0
    g4: ArcOfCircle CenterX=0 CenterY=94.0087 CenterZ=0 NormalX=0 NormalY=0 NormalZ=1 AngleXU=0 Radius=12 StartAngle=5.14216 EndAngle=10.5658
    g5: LineSegment StartX=-9.4 StartY=36.85 StartZ=0 EndX=-9.4 EndY=11.35 EndZ=0
    g6: LineSegment StartX=-9.4 StartY=11.35 StartZ=0 EndX=-12.2 EndY=11.35 EndZ=0
    g7: LineSegment StartX=-12.2 StartY=11.35 StartZ=0 EndX=-12.2 EndY=8.25 EndZ=0
    g8: LineSegment StartX=-12.2 StartY=8.25 StartZ=0 EndX=0 EndY=8.25 EndZ=0
    g9: LineSegment StartX=-10.7 StartY=78.1 StartZ=0 EndX=-6.5 EndY=78.1 EndZ=0
    g10: ArcOfCircle CenterX=-6.5 CenterY=79.6 CenterZ=0 NormalX=0 NormalY=0 NormalZ=1 AngleXU=0 Radius=1.5 StartAngle=4.71239 EndAngle=6.28319
    g11: LineSegment StartX=12.2 StartY=11.35 StartZ=0 EndX=9.4 EndY=11.35 EndZ=0
    g12: LineSegment StartX=9.4 StartY=11.35 StartZ=0 EndX=9.4 EndY=36.85 EndZ=0
    g13: LineSegment StartX=9.4 StartY=36.85 StartZ=0 EndX=12.2 EndY=36.85 EndZ=0
    g14: LineSegment StartX=12.2 StartY=36.85 StartZ=0 EndX=12.2 EndY=76.6 EndZ=0
    g15: ArcOfCircle CenterX=10.7 CenterY=76.6 CenterZ=0 NormalX=0 NormalY=0 NormalZ=1 AngleXU=0 Radius=1.5 StartAngle=-4.4e-15 EndAngle=1.5708
    g16: LineSegment StartX=10.7 StartY=78.1 StartZ=0 EndX=6.5 EndY=78.1 EndZ=0
    g17: ArcOfCircle CenterX=6.5 CenterY=79.6 CenterZ=0 NormalX=0 NormalY=0 NormalZ=1 AngleXU=0 Radius=1.5 StartAngle=3.14159 EndAngle=4.71239
    g18: LineSegment StartX=5 StartY=79.6 StartZ=0 EndX=5 EndY=83.1 EndZ=0
    g19: LineSegment StartX=12.2 StartY=11.35 StartZ=0 EndX=12.2 EndY=8.25 EndZ=0
    g20: LineSegment StartX=12.2 StartY=8.25 StartZ=0 EndX=0 EndY=8.25 EndZ=0
  constraints (56):
    c: Coincident(g-3,g0)
    c: Coincident(g0,g-3)
    c: Coincident(g0,g1)
    c: Vertical(g1)
    c: Tangent(g1,g2) = 1.5708
    c: Vertical(g3)
    c: Coincident(g0,g5)
    c: Vertical(g5)
    c: Coincident(g5,g6)
    c: Horizontal(g6)
    c: Coincident(g6,g7)
    c: Vertical(g7)
    c: Coincident(g7,g8)
    c: Horizontal(g8)
    c: Radius(g2) = 1.5
    c: Angle(g2) = 1.5708
    c: Coincident(g4,g3)
    c: DistanceX(g-2,g3) = -5
    c: DistanceY(g3,g3) = 3.5
    c: Tangent(g2,g9) = 1.5708
    c: Tangent(g9,g10) = -1.5708
    c: Tangent(g10,g3) = -1.5708
    c: Equal(g10,g2)
    c: Equal(g0,g6)
    c: DistanceY(g6,g-5) = 2.5
    c: DistanceY(g7,g7) = 3.1
    c: PointOnObject(g8,g-2)
    c: Horizontal(g11)
    c: Coincident(g11,g12)
    c: Coincident(g12,g-4)
    c: Vertical(g12)
    c: Coincident(g12,g13)
    c: Coincident(g13,g-4)
    c: Coincident(g13,g14)
    c: Vertical(g14)
    c: Tangent(g14,g15) = -1.5708
    c: Horizontal(g16)
    c: Tangent(g16,g17) = 1.5708
    c: Vertical(g18)
    c: Tangent(g15,g16) = -1.5708
    c: Equal(g15,g17)
    c: Equal(g17,g2)
    c: Tangent(g17,g18) = 1.5708
    c: Equal(g14,g1)
    c: Equal(g16,g9)
    c: Equal(g12,g5)
    c: Equal(g11,g6)
    c: Coincident(g11,g19)
    c: Vertical(g19)
    c: Coincident(g19,g20)
    c: Coincident(g20,g8)
    c: Horizontal(g20)
    c: Coincident(g18,g4)
    c: PointOnObject(g4,g-2)
    c: PointOnObject(g-9,g9)
    c: Diameter(g4) = 24
FEATURE [PartDesign::Pad] Pad011
  Direction = (0,-1,2e-16)
  Length = 2.8
  Length2 = 10
  Profile = -> Sketch011
  ReferenceAxis = -> Sketch011 [N_Axis]
  Type = 0
  expr: Length = Spreadsheet.acrylic_thin
FEATURE [PartDesign::Body] Body022  label="trunk"
  Group = -> [Binder017,Binder018,Binder019,Sketch011,Pad011]
  Origin = -> Origin025
  Tip = -> Pad011
FEATURE [PartDesign::SubShapeBinder] Binder020
  BindCopyOnChange = 0
  BindMode = 0
  ClaimChildren = false
  Context = -> Body023 [Binder020.]
  Fuse = false
  MakeFace = true
  OffsetFill = false
  OffsetIntersection = false
  OffsetJoinType = 0
  OffsetOpenResult = false
  PartialLoad = false
  Relative = true
  Support = -> [Body020]
  _Version = 2
FEATURE [PartDesign::SubShapeBinder] Binder021
  BindCopyOnChange = 0
  BindMode = 0
  ClaimChildren = false
  Context = -> Body023 [Binder021.]
  Fuse = false
  MakeFace = true
  OffsetFill = false
  OffsetIntersection = false
  OffsetJoinType = 0
  OffsetOpenResult = false
  PartialLoad = false
  Relative = true
  Support = -> [Body002]
  _Version = 2
FEATURE [PartDesign::Plane] DatumPlane004
  AttachmentOffset = pos=(0,0,0.1) rot=(0,0,1;0rad)
  Length = 148.256
  MapMode = 5
  Placement = pos=(-27.2,9e-15,1.36e-14) rot=(0.57735,-0.57735,-0.57735;2.0944rad)
  ResizeMode = 0
  Support = -> [Binder021]
  Width = 130.375
FEATURE [Sketcher::SketchObject] Sketch012
  ExternalGeometry = -> [Binder020,Binder021]
  FullyConstrained = true
  MapMode = 5
  Placement = pos=(-27.2,9e-15,1.36e-14) rot=(-0.57735,0.57735,0.57735;4.18879rad)
  Support = -> [DatumPlane004]
  sketch-geometry (34):
    g0: LineSegment StartX=-44.0703 StartY=62.2032 StartZ=0 EndX=-2.75559 EndY=81.4686 EndZ=0
    g1: LineSegment StartX=7.87582 StartY=77.5991 StartZ=0 EndX=23.7603 EndY=43.5348 EndZ=0
    g2: LineSegment StartX=27.747 StartY=42.0837 StartZ=0 EndX=61.2804 EndY=57.7206 EndZ=0
    g3: LineSegment StartX=61.2804 StartY=57.7206 StartZ=0 EndX=65.5066 EndY=48.6575 EndZ=0
    g4: LineSegment StartX=65.5066 StartY=48.6575 StartZ=0 EndX=31.9732 EndY=33.0207 EndZ=0
    g5: LineSegment StartX=14.6972 StartY=39.3086 StartZ=0 EndX=2.64634 EndY=65.1517 EndZ=0
    g6: LineSegment StartX=-6.75058 StartY=68.5719 StartZ=0 EndX=-39.8442 EndY=53.1402 EndZ=0
    g7: ArcOfCircle CenterX=-41.9572 CenterY=57.6717 CenterZ=0 NormalX=0 NormalY=0 NormalZ=1 AngleXU=0 Radius=5 StartAngle=2.00713 EndAngle=5.14872
    g8: ArcOfCircle CenterX=26.4792 CenterY=44.8027 CenterZ=0 NormalX=0 NormalY=0 NormalZ=1 AngleXU=0 Radius=3 StartAngle=3.57792 EndAngle=5.14872
    g9: LineSegment StartX=-44.0703 StartY=62.2032 StartZ=0 EndX=-39.8442 EndY=53.1402 EndZ=0
    g10: LineSegment StartX=-6.75058 StartY=68.5719 StartZ=0 EndX=2.64634 EndY=65.1517 EndZ=0
    g11: ArcOfCircle CenterX=26.4792 CenterY=44.8027 CenterZ=0 NormalX=0 NormalY=0 NormalZ=1 AngleXU=0 Radius=13 StartAngle=3.57792 EndAngle=5.14872
    g12: LineSegment StartX=-41.9572 StartY=57.6717 StartZ=0 EndX=-5.70494 EndY=74.5764 EndZ=0
    g13: LineSegment StartX=5.70494 StartY=70.4236 StartZ=0 EndX=22.6097 EndY=34.1713 EndZ=0
    g14: LineSegment StartX=22.6097 StartY=34.1713 StartZ=0 EndX=63.3935 EndY=53.1891 EndZ=0
    g15: LineSegment StartX=-5.70494 StartY=74.5764 StartZ=0 EndX=5.70494 EndY=70.4236 EndZ=0
    g16: LineSegment StartX=-1.92e-14 StartY=72.5 StartZ=0 EndX=-2.05212 EndY=66.8618 EndZ=0
    g17: Circle CenterX=-1.92e-14 CenterY=72.5 CenterZ=0 NormalX=0 NormalY=0 NormalZ=1 AngleXU=0 Radius=3
    g18: ArcOfCircle CenterX=0.625359 CenterY=74.2182 CenterZ=0 NormalX=0 NormalY=0 NormalZ=1 AngleXU=0 Radius=8 StartAngle=0.436332 EndAngle=2.00713
    g19: LineSegment StartX=71.0274 StartY=51.0155 StartZ=0 EndX=76.4652 EndY=53.5512 EndZ=0
    g20: LineSegment StartX=76.4652 StartY=53.5512 StartZ=0 EndX=76.9881 EndY=59.5284 EndZ=0
    g21: LineSegment StartX=76.9881 StartY=59.5284 StartZ=0 EndX=72.0732 EndY=62.9698 EndZ=0
    g22: LineSegment StartX=72.0732 StartY=62.9698 StartZ=0 EndX=66.6354 EndY=60.4341 EndZ=0
    g23: LineSegment StartX=66.6354 StartY=60.4341 StartZ=0 EndX=66.1124 EndY=54.4569 EndZ=0
    g24: LineSegment StartX=66.1124 StartY=54.4569 StartZ=0 EndX=71.0274 EndY=51.0155 EndZ=0
    g25: Circle CenterX=71.5503 CenterY=56.9926 CenterZ=0 NormalX=0 NormalY=0 NormalZ=1 AngleXU=0 Radius=6
    g26: LineSegment StartX=63.3935 StartY=53.1891 StartZ=0 EndX=66.1124 EndY=54.4569 EndZ=0
    g27: LineSegment StartX=72.0732 StartY=62.9698 StartZ=0 EndX=70.3828 EndY=66.595 EndZ=0
    g28: LineSegment StartX=70.3828 StartY=66.595 StartZ=0 EndX=61.7027 EndY=62.5475 EndZ=0
    g29: LineSegment StartX=61.7027 StartY=62.5475 StartZ=0 EndX=61.2804 EndY=57.7206 EndZ=0
    g30: LineSegment StartX=65.5066 StartY=48.6575 StartZ=0 EndX=69.4756 EndY=45.8784 EndZ=0
    g31: LineSegment StartX=69.4756 StartY=45.8784 StartZ=0 EndX=78.1557 EndY=49.926 EndZ=0
    g32: LineSegment StartX=78.1557 StartY=49.926 StartZ=0 EndX=76.4652 EndY=53.5512 EndZ=0
    g33: Circle CenterX=-41.9572 CenterY=57.6717 CenterZ=0 NormalX=0 NormalY=0 NormalZ=1 AngleXU=0 Radius=0.6
  constraints (84):
    c: Coincident(g2,g3)
    c: Coincident(g3,g4)
    c: Tangent(g6,g7) = 1.5708
    c: Tangent(g1,g8) = -1.5708
    c: Tangent(g2,g8) = -1.5708
    c: Perpendicular(g2,g3)
    c: Perpendicular(g4,g3)
    c: Perpendicular(g5,g4)
    c: Perpendicular(g2,g1)
    c: Tangent(g7,g0) = 1.5708
    c: Perpendicular(g5,g6)
    c: Angle(g7) = 3.14159
    c: Coincident(g9,g0)
    c: Coincident(g9,g6)
    c: Distance(g9) = 10
    c: Coincident(g10,g6)
    c: Coincident(g10,g5)
    c: Tangent(g11,g5) = 1.5708
    c: Tangent(g11,g4) = 1.5708
    c: Coincident(g11,g8)
    c: Symmetric(g2,g3,g14)
    c: Perpendicular(g14,g3)
    c: Coincident(g14,g13)
    c: Distance(g14) = 45
    c: Perpendicular(g13,g14)
    c: Perpendicular(g12,g13)
    c: Coincident(g12,g7)
    c: Angle(g10,g5) = 2.35619
    c: Coincident(g12,g15)
    c: Coincident(g13,g15)
    c: Perpendicular(g16,g10)
    c: Perpendicular(g16,g15)
    c: Symmetric(g6,g5,g16)
    c: Symmetric(g12,g13,g16)
    c: Coincident(g16,g-3)
    c: Equal(g12,g13)
    c: Distance(g12) = 40
    c: Coincident(g17,g16)
    c: Equal(g17,g-3)
    c: Tangent(g18,g1) = 1.5708
    c: Tangent(g18,g0) = 1.5708
    c: Equal(g3,g9)
    c: Coincident(g19,g20)
    c: Coincident(g20,g21)
    c: Coincident(g21,g22)
    c: Coincident(g22,g23)
    c: Coincident(g23,g24)
    c: Coincident(g24,g19)
    c: Equal(g19, g20-g24) x5
    c: PointOnObject(g19,g25)
    c: PointOnObject(g20,g25)
    c: PointOnObject(g21,g25)
    c: PointOnObject(g22,g25)
    c: PointOnObject(g23,g25)
    c: PointOnObject(g24,g25)
    c: Parallel(g22,g14)
    c: Coincident(g26,g14)
    c: Coincident(g26,g23)
    c: Perpendicular(g3,g26)
    c: Distance(g23) = 6
    c: Distance(g26) = 3
    c: Coincident(g22,g27)
    c: Coincident(g27,g28)
    c: Coincident(g28,g29)
    c: Coincident(g29,g2)
    c: Coincident(g4,g30)
    c: Coincident(g30,g31)
    c: Coincident(g31,g32)
    c: Coincident(g32,g19)
    c: Equal(g27,g32)
    c: Perpendicular(g22,g27)
    c: Perpendicular(g32,g19)
    c: Distance(g27) = 4
    c: Perpendicular(g28,g27)
    c: Perpendicular(g31,g32)
    c: Parallel(g24,g30)
    c: Parallel(g29,g23)
    c: Distance(g10) = 10
    c: Distance(g16) = 6
    c: Radius(g18) = 8
    c: Radius(g8) = 3
    c: Coincident(g33,g7)
    c: Diameter(g33) = 1.2
    c: Angle(g16) = -1.91986
FEATURE [PartDesign::Pad] Pad012
  Direction = (-1,-2e-16,-8e-16)
  Length = 2.8
  Length2 = 10
  Placement = pos=(-27.2,-1.2e-14,-2.9e-14) rot=(0.57735,-0.57735,-0.57735;2.0944rad)
  Profile = -> Sketch012
  ReferenceAxis = -> Sketch012 [N_Axis]
  Type = 0
  expr: Length = Spreadsheet.acrylic_thin
FEATURE [PartDesign::Body] Body023  label="arm_right"
  Group = -> [Binder020,Binder021,DatumPlane004,Sketch012,Pad012]
  Origin = -> Origin026
  Tip = -> Pad012
FEATURE [PartDesign::FeatureBase] Clone010
  BaseFeature = -> Body023
FEATURE [PartDesign::Body] Body024  label="arm_left"
  Group = -> [Clone010]
  Origin = -> Origin027
  Placement = pos=(57.2,30.65,6.9) rot=(1,0,0;0.436332rad)
  Tip = -> Clone010
FEATURE [Part::FeaturePython] Washer  label="M3-Washer"  # Fasteners workbench fastener (typed FeaturePython)
  Placement = pos=(-30.3,1.6e-14,72.5) rot=(0,-1,0;1.5708rad)
  baseObject = -> Body020 [Edge11]
  diameter = 1
  invert = false
  matchOuter = false
  offset = 0
  type = 11
FEATURE [Part::FeaturePython] Nut001  label="M3-Nut063"  # Fasteners workbench fastener (typed FeaturePython)
  Placement = pos=(-31.1,1.6e-14,72.5) rot=(0,-1,0;1.5708rad)
  baseObject = -> Washer [Edge1]
  diameter = 4
  invert = false
  leftHanded = false
  matchOuter = false
  offset = 0
  thread = false
  type = 25
FEATURE [Part::FeaturePython] Washer001  label="M3-Washer001"  # Fasteners workbench fastener (typed FeaturePython)
  Placement = pos=(30.3,-1.6e-14,72.5) rot=(0,1,0;1.5708rad)
  baseObject = -> Body021 [Edge11]
  diameter = 1
  invert = false
  matchOuter = false
  offset = 0
  type = 11
FEATURE [Part::FeaturePython] Nut002  label="M3-Nut064"  # Fasteners workbench fastener (typed FeaturePython)
  Placement = pos=(31.1,-1.6e-14,72.5) rot=(0,1,0;1.5708rad)
  baseObject = -> Washer001 [Edge1]
  diameter = 4
  invert = false
  leftHanded = false
  matchOuter = false
  offset = 0
  thread = false
  type = 25
FEATURE [Part::FeaturePython] Screw001  label="M1.6x10-Screw"  # Fasteners workbench fastener (typed FeaturePython)
  Placement = pos=(-21.3,1e-14,-9e-15) rot=(0,-1,0;1.5708rad)
  baseObject = -> Body003 [Edge18]
  diameter = 1
  invert = false
  leftHanded = false
  length = 5
  lengthCustom = 10
  matchOuter = false
  offset = 0
  thread = false
  type = 49
FEATURE [Part::FeaturePython] Screw002  label="M1.6x10-Screw001"  # Fasteners workbench fastener (typed FeaturePython)
  Placement = pos=(21.3,1e-14,1e-14) rot=(0,1,0;1.5708rad)
  baseObject = -> Body009 [Edge18]
  diameter = 1
  invert = false
  leftHanded = false
  length = 5
  lengthCustom = 10
  matchOuter = false
  offset = 0
  thread = false
  type = 49
FEATURE [Part::FeaturePython] Screw003  label="M3x14-Screw021"  # Fasteners workbench fastener (typed FeaturePython)
  Placement = pos=(-25.7,-1.09e-13,-53) rot=(0.969846,0.243717,0;3.14159rad)
  baseObject = -> Body007 [Edge86]
  diameter = 1
  invert = true
  leftHanded = false
  length = 6
  lengthCustom = 14
  matchOuter = false
  offset = 0
  thread = false
  type = 25
FEATURE [Part::FeaturePython] Nut003  label="M3-Nut060"  # Fasteners workbench fastener (typed FeaturePython)
  Placement = pos=(-25.7,-1.08e-13,-44.75) rot=(1,0,0;3.14159rad)
  baseObject = -> Screw003 [Edge71]
  diameter = 4
  invert = false
  leftHanded = false
  matchOuter = false
  offset = 5.75
  thread = false
  type = 25
FEATURE [Part::FeaturePython] Screw004  label="M3x14-Screw022"  # Fasteners workbench fastener (typed FeaturePython)
  Placement = pos=(25.7,-1.03e-13,-33) rot=(0.969846,-0.243717,0;3.14159rad)
  baseObject = -> Body015 [Edge87]
  diameter = 1
  invert = false
  leftHanded = false
  length = 6
  lengthCustom = 14
  matchOuter = false
  offset = 0
  thread = false
  type = 25
FEATURE [Part::FeaturePython] Nut004  label="M3-Nut061"  # Fasteners workbench fastener (typed FeaturePython)
  Placement = pos=(25.7,-1.04e-13,-24.75) rot=(1,0,0;3.14159rad)
  baseObject = -> Screw004 [Edge71]
  diameter = 4
  invert = false
  leftHanded = false
  matchOuter = false
  offset = 5.75
  thread = false
  type = 25
FEATURE [Part::FeaturePython] Screw005  label="M3x30-Screw"  # Fasteners workbench fastener (typed FeaturePython)
  Placement = pos=(-12.2,-8.9,20.85) rot=(0,-1,0;1.5708rad)
  baseObject = -> Body017 [Edge105]
  diameter = 1
  invert = false
  leftHanded = false
  length = 10
  lengthCustom = 30
  matchOuter = false
  offset = 0
  thread = false
  type = 25
FEATURE [Part::FeaturePython] Nut005  label="M3-Nut065"  # Fasteners workbench fastener (typed FeaturePython)
  Placement = pos=(12.2,-8.9,20.85) rot=(0,1,0;1.5708rad)
  baseObject = -> Body018 [Edge104]
  diameter = 4
  invert = true
  leftHanded = false
  matchOuter = false
  offset = 0
  thread = false
  type = 25
FEATURE [Part::FeaturePython] Screw006  label="M3x30-Screw001"  # Fasteners workbench fastener (typed FeaturePython)
  Placement = pos=(-12.2,8.9,20.85) rot=(0,-1,0;1.5708rad)
  baseObject = -> Body017 [Edge108]
  diameter = 1
  invert = false
  leftHanded = false
  length = 10
  lengthCustom = 30
  matchOuter = false
  offset = 0
  thread = false
  type = 25
FEATURE [Part::FeaturePython] Nut006  label="M3-Nut066"  # Fasteners workbench fastener (typed FeaturePython)
  Placement = pos=(12.2,8.9,20.85) rot=(0,1,0;1.5708rad)
  baseObject = -> Body018 [Edge107]
  diameter = 4
  invert = true
  leftHanded = false
  matchOuter = false
  offset = 0
  thread = false
  type = 25
FEATURE [App::DocumentObjectGroup] Group001  label="3D_prints"
  Group = -> [Body005,Body011,Body019,Body020,Body021]
FEATURE [Part::FeaturePython] Screw007  label="M3x14-Screw023"  # Fasteners workbench fastener (typed FeaturePython)
  Placement = pos=(15.5,-2.165e-12,10) rot=(0,-1,0;1.5708rad)
  baseObject = -> Body011 [Edge6]
  diameter = 1
  invert = false
  leftHanded = false
  length = 6
  lengthCustom = 14
  matchOuter = false
  offset = 0
  thread = false
  type = 25
FEATURE [Part::FeaturePython] Nut007  label="M3-Nut062"  # Fasteners workbench fastener (typed FeaturePython)
  Placement = pos=(29.5,-2.168e-12,10) rot=(0,-1,0;1.5708rad)
  baseObject = -> Screw007 [Edge71]
  diameter = 4
  invert = false
  leftHanded = false
  matchOuter = false
  offset = 0
  thread = false
  type = 25
FEATURE [App::DocumentObjectGroup] Group  label="Fasteners"
  Group = -> [Washer,Nut001,Washer001,Nut002,ThreadedRod,Screw,Nut,Screw001,Screw002,Screw003,Nut003,Screw004,Nut004,Screw005,Nut005,Screw006,Nut006,Screw007,Nut007]
FEATURE [PartDesign::SubShapeBinder] Binder022
  BindCopyOnChange = 0
  BindMode = 0
  ClaimChildren = false
  Context = -> Body025 [Binder022.]
  Fuse = false
  MakeFace = true
  OffsetFill = false
  OffsetIntersection = false
  OffsetJoinType = 0
  OffsetOpenResult = false
  PartialLoad = false
  Relative = true
  Support = -> [Body017[Pad007.]]
  _Version = 2
FEATURE [Sketcher::SketchObject] Sketch013
  ExternalGeometry = -> [Binder022]
  FullyConstrained = true
  MapMode = 5
  Placement = pos=(0,0,0) rot=(0.57735,0.57735,0.57735;2.0944rad)
  Support = -> [YZ_Plane026]
  sketch-geometry (4):
    g0: LineSegment StartX=38.15 StartY=36.85 StartZ=0 EndX=40.15 EndY=36.85 EndZ=0
    g1: LineSegment StartX=40.15 StartY=36.85 StartZ=0 EndX=40.15 EndY=35.85 EndZ=0
    g2: LineSegment StartX=40.15 StartY=35.85 StartZ=0 EndX=38.15 EndY=35.85 EndZ=0
    g3: LineSegment StartX=38.15 StartY=35.85 StartZ=0 EndX=38.15 EndY=36.85 EndZ=0
  constraints (11):
    c: Coincident(g0,g1)
    c: Coincident(g1,g2)
    c: Coincident(g2,g3)
    c: Coincident(g3,g0)
    c: Horizontal(g0)
    c: Horizontal(g2)
    c: Vertical(g1)
    c: Vertical(g3)
    c: DistanceX(g0,g0) = 2
    c: DistanceY(g1,g1) = 1
    c: Symmetric(g2,g1,g-3)
FEATURE [PartDesign::Pad] Pad013
  Direction = (1,-2e-16,3e-16)
  Length = 22.5
  Length2 = 10
  Midplane = true
  Placement = pos=(0,0,0) rot=(0.57735,0.57735,0.57735;2.0944rad)
  Profile = -> Sketch013
  ReferenceAxis = -> Sketch013 [N_Axis]
  Type = 0
FEATURE [PartDesign::FeaturePython] Bend  # WARN: FeaturePython — macro-defined, semantics opaque (R4)
  AutoMiter = true
  BaseFeature = -> Pad013
  BendType = 0
  LengthList = [26]
  LengthSpec = 0
  ReliefFactor = 0.7
  UseReliefFactor = false
  angle = 90
  baseObject = -> Pad013 [Face5]
  bendAList = [90]
  extend1 = 0
  extend2 = 0
  gap1 = 0
  gap2 = 0
  invert = false
  kfactor = 0.5
  length = 26
  maxExtendDist = 5
  minGap = 0.2
  minReliefGap = 1
  miterangle1 = 0
  miterangle2 = 0
  offset = 0
  radius = 1
  reliefType = 0
  reliefd = 1
  reliefw = 0.8
  sketchflip = false
  sketchinvert = false
  unfold = false
FEATURE [PartDesign::FeaturePython] Bend001  # WARN: FeaturePython — macro-defined, semantics opaque (R4)
  AutoMiter = true
  BaseFeature = -> Bend
  BendType = 0
  LengthList = [22.5]
  LengthSpec = 0
  ReliefFactor = 0.7
  UseReliefFactor = false
  angle = 90
  baseObject = -> Bend [Face3]
  bendAList = [90]
  extend1 = 0
  extend2 = 0
  gap1 = 0
  gap2 = 0
  invert = false
  kfactor = 0.5
  length = 22.5
  maxExtendDist = 5
  minGap = 0.2
  minReliefGap = 1
  miterangle1 = 0
  miterangle2 = 0
  offset = 0
  radius = 1
  reliefType = 0
  reliefd = 1
  reliefw = 0.8
  sketchflip = false
  sketchinvert = false
  unfold = false
FEATURE [PartDesign::SubShapeBinder] Binder023
  BindCopyOnChange = 0
  BindMode = 0
  ClaimChildren = false
  Context = -> Body025 [Binder023.]
  Fuse = false
  MakeFace = true
  OffsetFill = false
  OffsetIntersection = false
  OffsetJoinType = 0
  OffsetOpenResult = false
  PartialLoad = false
  Relative = true
  Support = -> [Body018[Clone008.]]
  _Version = 2
FEATURE [PartDesign::FeaturePython] Bend002  # WARN: FeaturePython — macro-defined, semantics opaque (R4)
  AutoMiter = true
  BaseFeature = -> Bend001
  BendType = 0
  LengthList = [26]
  LengthSpec = 0
  ReliefFactor = 0.7
  UseReliefFactor = false
  angle = 90
  baseObject = -> Bend001 [Face3]
  bendAList = [90]
  extend1 = 0
  extend2 = 0
  gap1 = 0
  gap2 = 0
  invert = false
  kfactor = 0.5
  length = 26
  maxExtendDist = 5
  minGap = 0.2
  minReliefGap = 1
  miterangle1 = 0
  miterangle2 = 0
  offset = 0
  radius = 1
  reliefType = 0
  reliefd = 1
  reliefw = 0.8
  sketchflip = false
  sketchinvert = false
  unfold = false
FEATURE [PartDesign::FeaturePython] Bend003  # WARN: FeaturePython — macro-defined, semantics opaque (R4)
  AutoMiter = true
  BaseFeature = -> Bend002
  BendType = 0
  LengthList = [0.1]
  LengthSpec = 0
  ReliefFactor = 0.7
  UseReliefFactor = false
  angle = 90
  baseObject = -> Bend002 [Face3]
  bendAList = [90]
  extend1 = 0
  extend2 = 0
  gap1 = 0
  gap2 = 0
  invert = false
  kfactor = 0.5
  length = 0.1
  maxExtendDist = 5
  minGap = 0.2
  minReliefGap = 1
  miterangle1 = 0
  miterangle2 = 0
  offset = 0
  radius = 1
  reliefType = 0
  reliefd = 1
  reliefw = 0.8
  sketchflip = false
  sketchinvert = false
  unfold = false
FEATURE [PartDesign::Fillet] Fillet002
  Base = -> Bend003 [Edge1,Edge2,Edge3,Edge4,Edge5,Edge6,Edge7,Edge8,Edge9,Edge10,Edge11,Edge12,Edge13,Edge14,Edge15,Edge16,Edge17,Edge18,Edge19,Edge20,Edge21,Edge22,Edge23,Edge24,Edge25,Edge26,Edge27,Edge28,Edge29,Edge30,Edge31,Edge32,Edge33,Edge34,Edge35,Edge36,Edge37,Edge38,Edge39,Edge40,+32 more]
  BaseFeature = -> Bend003
  Radius = 0.4
  Refine = true
  SupportTransform = false
  UseAllEdges = true
FEATURE [PartDesign::Body] Body025  label="elastic_band"
  Group = -> [Binder022,Sketch013,Pad013,Bend,Bend001,Binder023,Bend002,Bend003,Fillet002]
  Origin = -> Origin028
  Tip = -> Fillet002
FEATURE [PartDesign::SubShapeBinder] Binder024
  BindCopyOnChange = 0
  BindMode = 0
  ClaimChildren = false
  Context = -> Body026 [Binder024.]
  Fuse = false
  MakeFace = true
  OffsetFill = false
  OffsetIntersection = false
  OffsetJoinType = 0
  OffsetOpenResult = false
  PartialLoad = false
  Relative = true
  Support = -> [Body017[Pad007.]]
  _Version = 2
FEATURE [Sketcher::SketchObject] Sketch014
  ExternalGeometry = -> [Binder024]
  FullyConstrained = true
  MapMode = 5
  Placement = pos=(-9.4,0,0) rot=(0.57735,0.57735,0.57735;2.0944rad)
  Support = -> [Binder024]
  sketch-geometry (10):
    g0: ArcOfCircle CenterX=14.15 CenterY=31.85 CenterZ=0 NormalX=0 NormalY=0 NormalZ=1 AngleXU=0 Radius=3 StartAngle=1.5708 EndAngle=3.14159
    g1: LineSegment StartX=14.15 StartY=34.85 StartZ=0 EndX=39.15 EndY=34.85 EndZ=0
    g2: ArcOfCircle CenterX=39.15 CenterY=31.85 CenterZ=0 NormalX=0 NormalY=0 NormalZ=1 AngleXU=0 Radius=3 StartAngle=1e-16 EndAngle=1.5708
    g3: LineSegment StartX=42.15 StartY=31.85 StartZ=0 EndX=42.15 EndY=11.85 EndZ=0
    g4: ArcOfCircle CenterX=39.15 CenterY=11.85 CenterZ=0 NormalX=0 NormalY=0 NormalZ=1 AngleXU=0 Radius=3 StartAngle=4.71239 EndAngle=6.28319
    g5: LineSegment StartX=39.15 StartY=8.85 StartZ=0 EndX=14.15 EndY=8.85 EndZ=0
    g6: ArcOfCircle CenterX=14.15 CenterY=11.85 CenterZ=0 NormalX=0 NormalY=0 NormalZ=1 AngleXU=0 Radius=3 StartAngle=3.14159 EndAngle=4.71239
    g7: LineSegment StartX=11.15 StartY=11.85 StartZ=0 EndX=11.15 EndY=31.85 EndZ=0
    g8: GeomPoint X=11.15 Y=34.85 Z=0
    g9: GeomPoint X=42.15 Y=8.85 Z=0
  constraints (24):
    c: Tangent(g0,g1) = 1.5708
    c: Tangent(g1,g2) = 1.5708
    c: Tangent(g2,g3) = 1.5708
    c: Tangent(g3,g4) = 1.5708
    c: Tangent(g4,g5) = 1.5708
    c: Tangent(g5,g6) = 1.5708
    c: Tangent(g6,g7) = 1.5708
    c: Tangent(g7,g0) = 1.5708
    c: Horizontal(g1)
    c: Horizontal(g5)
    c: Vertical(g3)
    c: Vertical(g7)
    c: Equal(g0,g2)
    c: Equal(g2,g4)
    c: Equal(g4,g6)
    c: PointOnObject(g8,g1)
    c: PointOnObject(g8,g7)
    c: PointOnObject(g9,g3)
    c: PointOnObject(g9,g5)
    c: Radius(g0) = 3
    c: PointOnObject(g2,g-4)
    c: Vertical(g0,g-3)
    c: PointOnObject(g1,g-5)
    c: PointOnObject(g4,g-6)
FEATURE [PartDesign::Pad] Pad014
  Direction = (1,0,0)
  Length = 1
  Length2 = 10
  Profile = -> Sketch014
  ReferenceAxis = -> Sketch014 [N_Axis]
  Type = 0
FEATURE [PartDesign::Body] Body026  label="foam_battery_right"
  Group = -> [Binder024,Sketch014,Pad014]
  Origin = -> Origin029
  Tip = -> Pad014
FEATURE [PartDesign::FeatureBase] Clone011
  BaseFeature = -> Body026
FEATURE [PartDesign::Body] Body027  label="foam_battery_left"
  Group = -> [Clone011]
  Origin = -> Origin030
  Placement = pos=(17.8,0,0) rot=(0,0,1;0rad)
  Tip = -> Clone011
FEATURE [PartDesign::SubShapeBinder] Binder025
  BindCopyOnChange = 0
  BindMode = 0
  ClaimChildren = false
  Context = -> Body028 [Binder025.]
  Fuse = false
  MakeFace = true
  OffsetFill = false
  OffsetIntersection = false
  OffsetJoinType = 0
  OffsetOpenResult = false
  PartialLoad = false
  Relative = true
  Support = -> [Body007[Pad006.]]
  _Version = 2
FEATURE [Sketcher::SketchObject] Sketch015
  ExternalGeometry = -> [Binder025]
  FullyConstrained = true
  MapMode = 5
  Placement = pos=(2.92e-14,-1.081e-13,-53) rot=(1,0,0;3.14159rad)
  Support = -> [Binder025]
  sketch-geometry (21):
    g0: LineSegment StartX=-25.7 StartY=44 StartZ=0 EndX=12.3 EndY=44 EndZ=0
    g1: ArcOfCircle CenterX=12.3 CenterY=40 CenterZ=0 NormalX=0 NormalY=0 NormalZ=1 AngleXU=0 Radius=4 StartAngle=4.71239 EndAngle=7.85398
    g2: LineSegment StartX=12.3 StartY=36 StartZ=0 EndX=-15.7 EndY=36 EndZ=0
    g3: ArcOfCircle CenterX=-15.7 CenterY=31 CenterZ=0 NormalX=0 NormalY=0 NormalZ=1 AngleXU=0 Radius=5 StartAngle=1.5708 EndAngle=3.14159
    g4: LineSegment StartX=-20.7 StartY=31 StartZ=0 EndX=-20.7 EndY=16.345 EndZ=0
    g5: ArcOfCircle CenterX=-25.7 CenterY=10.1 CenterZ=0 NormalX=0 NormalY=0 NormalZ=1 AngleXU=0 Radius=8 StartAngle=1e-16 EndAngle=0.895665
    g6: LineSegment StartX=-17.7 StartY=10.1 StartZ=0 EndX=-17.7 EndY=-9.9 EndZ=0
    g7: ArcOfCircle CenterX=-25.7 CenterY=-9.9 CenterZ=0 NormalX=0 NormalY=0 NormalZ=1 AngleXU=0 Radius=8 StartAngle=5.38752 EndAngle=6.28319
    g8: LineSegment StartX=-20.7 StartY=-16.145 StartZ=0 EndX=-20.7 EndY=-47 EndZ=0
    g9: ArcOfCircle CenterX=-15.7 CenterY=-47 CenterZ=0 NormalX=0 NormalY=0 NormalZ=1 AngleXU=0 Radius=5 StartAngle=3.14159 EndAngle=4.71239
    g10: LineSegment StartX=-15.7 StartY=-52 StartZ=0 EndX=12.3 EndY=-52 EndZ=0
    g11: ArcOfCircle CenterX=12.3 CenterY=-56 CenterZ=0 NormalX=0 NormalY=0 NormalZ=1 AngleXU=0 Radius=4 StartAngle=4.71239 EndAngle=7.85398
    g12: LineSegment StartX=12.3 StartY=-60 StartZ=0 EndX=-25.7 EndY=-60 EndZ=0
    g13: ArcOfCircle CenterX=-25.7 CenterY=-55 CenterZ=0 NormalX=0 NormalY=0 NormalZ=1 AngleXU=0 Radius=5 StartAngle=3.14159 EndAngle=4.71239
    g14: LineSegment StartX=-30.7 StartY=-55 StartZ=0 EndX=-30.7 EndY=-16.145 EndZ=0
    g15: ArcOfCircle CenterX=-25.7 CenterY=-9.9 CenterZ=0 NormalX=0 NormalY=0 NormalZ=1 AngleXU=0 Radius=8 StartAngle=3.14159 EndAngle=4.03726
    g16: LineSegment StartX=-33.7 StartY=-9.9 StartZ=0 EndX=-33.7 EndY=10.1 EndZ=0
    g17: ArcOfCircle CenterX=-25.7 CenterY=10.1 CenterZ=0 NormalX=0 NormalY=0 NormalZ=1 AngleXU=0 Radius=8 StartAngle=2.24593 EndAngle=3.14159
    g18: LineSegment StartX=-30.7 StartY=16.345 StartZ=0 EndX=-30.7 EndY=39 EndZ=0
    g19: ArcOfCircle CenterX=-25.7 CenterY=39 CenterZ=0 NormalX=0 NormalY=0 NormalZ=1 AngleXU=0 Radius=5 StartAngle=1.5708 EndAngle=3.14159
    g20: Circle CenterX=-25.7 CenterY=0 CenterZ=0 NormalX=0 NormalY=0 NormalZ=1 AngleXU=0 Radius=4.5
  constraints (46):
    c: Horizontal(g0)
    c: Tangent(g0,g1) = 1.5708
    c: Horizontal(g2)
    c: Tangent(g2,g3) = -1.5708
    c: Vertical(g6)
    c: Tangent(g6,g7) = 1.5708
    c: Vertical(g8)
    c: Tangent(g8,g9) = -1.5708
    c: Horizontal(g10)
    c: Tangent(g10,g11) = 1.5708
    c: Tangent(g11,g12) = 1.5708
    c: Vertical(g14)
    c: Vertical(g16)
    c: Tangent(g16,g17) = 1.5708
    c: Vertical(g18)
    c: Tangent(g18,g19) = 1.5708
    c: Tangent(g19,g0) = 1.5708
    c: Tangent(g1,g2) = 1.5708
    c: Tangent(g3,g4) = -1.5708
    c: Tangent(g5,g6) = 1.5708
    c: Coincident(g17,g18)
    c: Coincident(g4,g5)
    c: Vertical(g4)
    c: Coincident(g7,g8)
    c: Tangent(g9,g10) = -1.5708
    c: Tangent(g13,g14) = 1.5708
    c: Coincident(g14,g15)
    c: Tangent(g15,g16) = 1.5708
    c: Coincident(g19,g-7)
    c: Coincident(g1,g-3)
    c: Coincident(g3,g-8)
    c: Coincident(g5,g-11)
    c: Coincident(g5,g17)
    c: Coincident(g7,g-13)
    c: Coincident(g15,g7)
    c: Coincident(g9,g-5)
    c: Coincident(g11,g-4)
    c: Coincident(g13,g-6)
    c: Equal(g1,g-3)
    c: Equal(g-11,g5)
    c: Equal(g-5,g9)
    c: Tangent(g12,g13) = 1.5708
    c: Equal(g13,g-6)
    c: Equal(g15,g-13)
    c: Coincident(g20,g-9)
    c: Diameter(g20) = 9
FEATURE [PartDesign::Pad] Pad015
  Direction = (5e-16,-2.2e-15,-1)
  Length = 2
  Length2 = 10
  Profile = -> Sketch015
  ReferenceAxis = -> Sketch015 [N_Axis]
  Type = 0
FEATURE [PartDesign::Body] Body028  label="foam_feet_right"
  Group = -> [Binder025,Sketch015,Pad015]
  Origin = -> Origin031
  Tip = -> Pad015
FEATURE [PartDesign::FeatureBase] Clone012
  BaseFeature = -> Body028
FEATURE [PartDesign::Body] Body029  label="foam_feet_left"
  Group = -> [Clone012]
  Origin = -> Origin032
  Placement = pos=(1.1e-14,0,-88) rot=(0,1,0;3.14159rad)
  Tip = -> Clone012
FEATURE [Part::Part2DObjectPython] Shape2DView  label="foam_battery_right_DXF"  # Draft 2D object (typed FeaturePython)
  AutoUpdate = true
  Base = -> Body026
  Clip = false
  FuseArch = false
  HiddenLines = false
  InPlace = true
  OnlySolids = false
  Projection = (-1,0,0)
  ProjectionMode = 0
  SegmentLength = 0.05
  Tessellation = false
  VisibleOnly = false
FEATURE [Part::Part2DObjectPython] Shape2DView001  label="foam_feet_right_DXF"  # Draft 2D object (typed FeaturePython)
  AutoUpdate = true
  Base = -> Body028
  Clip = false
  FuseArch = false
  HiddenLines = false
  InPlace = true
  OnlySolids = false
  Projection = (0,0,1)
  ProjectionMode = 0
  SegmentLength = 0.05
  Tessellation = false
  VisibleOnly = false
FEATURE [Part::Part2DObjectPython] Shape2DView002  label="foam_feet_left_DXF"  # Draft 2D object (typed FeaturePython)
  AutoUpdate = true
  Base = -> Body029
  Clip = false
  FuseArch = false
  HiddenLines = false
  InPlace = true
  OnlySolids = false
  Projection = (0,0,1)
  ProjectionMode = 0
  SegmentLength = 0.05
  Tessellation = false
  VisibleOnly = false
FEATURE [Part::Part2DObjectPython] Shape2DView003  label="foam_battery_left_DXF"  # Draft 2D object (typed FeaturePython)
  AutoUpdate = true
  Base = -> Body027
  Clip = false
  FuseArch = false
  HiddenLines = false
  InPlace = true
  OnlySolids = false
  Projection = (-1,0,0)
  ProjectionMode = 0
  SegmentLength = 0.05
  Tessellation = false
  VisibleOnly = false
FEATURE [Part::Part2DObjectPython] Shape2DView004  label="cam_right_1_DXF"  # Draft 2D object (typed FeaturePython)
  AutoUpdate = true
  Base = -> Body
  Clip = false
  FuseArch = false
  HiddenLines = false
  InPlace = true
  OnlySolids = false
  Projection = (-1,0,0)
  ProjectionMode = 0
  SegmentLength = 0.05
  Tessellation = false
  VisibleOnly = false
FEATURE [Part::Part2DObjectPython] Shape2DView005  label="cam_right_2_DXF"  # Draft 2D object (typed FeaturePython)
  AutoUpdate = true
  Base = -> Body003
  Clip = false
  FuseArch = false
  HiddenLines = false
  InPlace = true
  OnlySolids = false
  Projection = (-1,0,0)
  ProjectionMode = 0
  SegmentLength = 0.05
  Tessellation = false
  VisibleOnly = false
FEATURE [Part::Part2DObjectPython] Shape2DView006  label="cam_right_3_DXF"  # Draft 2D object (typed FeaturePython)
  AutoUpdate = true
  Base = -> Body004
  Clip = false
  FuseArch = false
  HiddenLines = false
  InPlace = true
  OnlySolids = false
  Projection = (-1,0,0)
  ProjectionMode = 0
  SegmentLength = 0.05
  Tessellation = false
  VisibleOnly = false
FEATURE [Part::Part2DObjectPython] Shape2DView008  label="cam_left_1_DXF"  # Draft 2D object (typed FeaturePython)
  AutoUpdate = true
  Base = -> Body008
  Clip = false
  FuseArch = false
  HiddenLines = false
  InPlace = true
  OnlySolids = false
  Projection = (1,0,0)
  ProjectionMode = 0
  SegmentLength = 0.05
  Tessellation = false
  VisibleOnly = false
FEATURE [Part::Part2DObjectPython] Shape2DView009  label="cam_left_2_DXF"  # Draft 2D object (typed FeaturePython)
  AutoUpdate = true
  Base = -> Body009
  Clip = false
  FuseArch = false
  HiddenLines = false
  InPlace = true
  OnlySolids = false
  Projection = (1,0,0)
  ProjectionMode = 0
  SegmentLength = 0.05
  Tessellation = false
  VisibleOnly = false
FEATURE [Part::Part2DObjectPython] Shape2DView010  label="cam_left_3_DXF"  # Draft 2D object (typed FeaturePython)
  AutoUpdate = true
  Base = -> Body010
  Clip = false
  FuseArch = false
  HiddenLines = false
  InPlace = true
  OnlySolids = false
  Projection = (1,0,0)
  ProjectionMode = 0
  SegmentLength = 0.05
  Tessellation = false
  VisibleOnly = false
FEATURE [Part::Part2DObjectPython] Shape2DView012  label="feet_right_DXF"  # Draft 2D object (typed FeaturePython)
  AutoUpdate = true
  Base = -> Body007
  Clip = false
  FuseArch = false
  HiddenLines = false
  InPlace = true
  OnlySolids = false
  Projection = (0,0,1)
  ProjectionMode = 0
  SegmentLength = 0.05
  Tessellation = false
  VisibleOnly = false
FEATURE [Part::Part2DObjectPython] Shape2DView013  label="feet_left_DXF"  # Draft 2D object (typed FeaturePython)
  AutoUpdate = true
  Base = -> Body015
  Clip = false
  FuseArch = false
  HiddenLines = false
  InPlace = true
  OnlySolids = false
  Projection = (0,0,1)
  ProjectionMode = 0
  SegmentLength = 0.05
  Tessellation = false
  VisibleOnly = false
FEATURE [Part::Part2DObjectPython] Shape2DView014  label="body_right_DXF"  # Draft 2D object (typed FeaturePython)
  AutoUpdate = true
  Base = -> Body017
  Clip = false
  FuseArch = false
  HiddenLines = false
  InPlace = true
  OnlySolids = false
  Projection = (-1,0,0)
  ProjectionMode = 0
  SegmentLength = 0.05
  Tessellation = false
  VisibleOnly = false
FEATURE [Part::Part2DObjectPython] Shape2DView015  label="body_left_DXF"  # Draft 2D object (typed FeaturePython)
  AutoUpdate = true
  Base = -> Body018
  Clip = false
  FuseArch = false
  HiddenLines = false
  InPlace = true
  OnlySolids = false
  Projection = (1,0,0)
  ProjectionMode = 0
  SegmentLength = 0.05
  Tessellation = false
  VisibleOnly = false
FEATURE [Part::Part2DObjectPython] Shape2DView016  label="arm_right_DXF"  # Draft 2D object (typed FeaturePython)
  AutoUpdate = true
  Base = -> Body024
  Clip = false
  FuseArch = false
  HiddenLines = false
  InPlace = true
  OnlySolids = false
  Projection = (1,0,0)
  ProjectionMode = 0
  SegmentLength = 0.05
  Tessellation = false
  VisibleOnly = false
FEATURE [Part::Part2DObjectPython] Shape2DView018  label="trunk_DXF"  # Draft 2D object (typed FeaturePython)
  AutoUpdate = true
  Base = -> Body022
  Clip = false
  FuseArch = false
  HiddenLines = false
  InPlace = true
  OnlySolids = false
  Projection = (0,-1,0)
  ProjectionMode = 0
  SegmentLength = 0.05
  Tessellation = false
  VisibleOnly = false
FEATURE [Part::Part2DObjectPython] Shape2DView019  label="arm_left_DXF"  # Draft 2D object (typed FeaturePython)
  AutoUpdate = true
  Base = -> Body024
  Clip = false
  FuseArch = false
  HiddenLines = false
  InPlace = true
  OnlySolids = false
  Projection = (-1,0,0)
  ProjectionMode = 0
  SegmentLength = 0.05
  Tessellation = false
  VisibleOnly = false
FEATURE [Spreadsheet::Sheet] Fasteners_BOM
  cells = A1='Type; B1='Qty; A2='DIN967 Screw M3x14; B2=4; A3='DIN967 Screw M3x30; B3=2; A4='ISO4032 Nut M3; B4=8; A5='ISO7045 Screw M1.6x10; B5=2; A6='ISO7093-1 Washer M3; B6=2; A7='Threaded Rod M3x70; B7=1
FEATURE [PartDesign::SubShapeBinder] Binder028
  BindCopyOnChange = 0
  BindMode = 0
  ClaimChildren = false
  Context = -> Body030 [Binder028.]
  Fuse = false
  MakeFace = true
  OffsetFill = false
  OffsetIntersection = false
  OffsetJoinType = 0
  OffsetOpenResult = false
  PartialLoad = false
  Relative = true
  Support = -> [Body024]
  _Version = 2
FEATURE [PartDesign::SubShapeBinder] Binder029
  BindCopyOnChange = 0
  BindMode = 0
  ClaimChildren = false
  Context = -> Body030 [Binder029.]
  Fuse = false
  MakeFace = true
  OffsetFill = false
  OffsetIntersection = false
  OffsetJoinType = 0
  OffsetOpenResult = false
  PartialLoad = false
  Relative = true
  Support = -> [Body014]
  _Version = 2
FEATURE [Sketcher::SketchObject] Sketch016
  ExternalGeometry = -> [Binder028,Binder029]
  FullyConstrained = true
  MapMode = 5
  Placement = pos=(27.1,3.3e-15,1.4e-15) rot=(0.57735,0.57735,0.57735;2.0944rad)
  Support = -> [Binder029]
  sketch-geometry (3):
    g0: LineSegment StartX=43.8765 StartY=76.4783 StartZ=0 EndX=7.42656 EndY=40.422 EndZ=0
    g1: LineSegment StartX=7.42656 StartY=40.422 StartZ=0 EndX=7 EndY=40 EndZ=0
    g2: LineSegment StartX=43.8765 StartY=76.4783 StartZ=0 EndX=44.3031 EndY=76.9002 EndZ=0
  constraints (8):
    c: Coincident(g1,g0)
    c: Parallel(g1,g0)
    c: Coincident(g2,g0)
    c: Parallel(g2,g0)
    c: Coincident(g1,g-4)
    c: PointOnObject(g0,g-4)
    c: Coincident(g2,g-3)
    c: PointOnObject(g0,g-3)
FEATURE [PartDesign::Plane] DatumPlane005
  AttachmentOffset = pos=(0,0,0) rot=(1,0,0;1.5708rad)
  Length = 72.3981
  MapMode = 7
  Placement = pos=(27.1,43.8765,76.4783) rot=(0,0.924915,0.380174;3.14159rad)
  ResizeMode = 0
  Support = -> [Sketch016]
  Width = 138.227
FEATURE [Sketcher::SketchObject] Sketch017
  ExternalGeometry = -> [Binder028,Binder029]
  FullyConstrained = true
  MapMode = 5
  Placement = pos=(27.1,43.8765,76.4783) rot=(0,0.924915,0.380174;3.14159rad)
  Support = -> [DatumPlane005]
  sketch-geometry (9):
    g0: LineSegment StartX=-3.3e-14 StartY=-52.3704 StartZ=0 EndX=2.8 EndY=-52.3704 EndZ=0
    g1: LineSegment StartX=-2.9 StartY=0.6 StartZ=0 EndX=-0.1 EndY=0.6 EndZ=0
    g2: ArcOfCircle CenterX=2.8 CenterY=-51.8704 CenterZ=0 NormalX=0 NormalY=0 NormalZ=1 AngleXU=0 Radius=0.5 StartAngle=4.71239 EndAngle=6.28319
    g3: LineSegment StartX=3.3 StartY=-51.8704 StartZ=0 EndX=3.3 EndY=-47.8704 EndZ=0
    g4: ArcOfCircle CenterX=-2.9 CenterY=0.1 CenterZ=0 NormalX=0 NormalY=0 NormalZ=1 AngleXU=0 Radius=0.5 StartAngle=1.5708 EndAngle=3.14159
    g5: LineSegment StartX=-3.4 StartY=0.1 StartZ=0 EndX=-3.4 EndY=-3.9 EndZ=0
    g6: ArcOfCircle CenterX=-0.1 CenterY=0.1 CenterZ=0 NormalX=0 NormalY=0 NormalZ=1 AngleXU=0 Radius=0.5 StartAngle=6.26587 EndAngle=7.85398
    g7: ArcOfCircle CenterX=-3.55e-14 CenterY=-51.8704 CenterZ=0 NormalX=0 NormalY=0 NormalZ=1 AngleXU=0 Radius=0.5 StartAngle=3.12427 EndAngle=4.71239
    g8: LineSegment StartX=-0.499925 StartY=-51.8618 StartZ=0 EndX=0.399925 EndY=0.0913411 EndZ=0
  constraints (20):
    c: Tangent(g2,g0) = -1.5708
    c: Tangent(g3,g2) = -1.5708
    c: Radius(g2) = 0.5
    c: Perpendicular(g0,g3)
    c: Distance(g3) = 4
    c: Tangent(g4,g1) = 1.5708
    c: Perpendicular(g5,g1)
    c: Equal(g4,g2)
    c: Equal(g3,g5)
    c: Tangent(g4,g5) = -1.5708
    c: Tangent(g0,g7) = -1.5708
    c: Tangent(g6,g1) = 1.5708
    c: Equal(g6,g4)
    c: Equal(g7,g2)
    c: Tangent(g6,g8) = -1.5708
    c: Tangent(g8,g7) = 1.5708
    c: Symmetric(g-5,g-5,g7)
    c: Symmetric(g-6,g-6,g2)
    c: Symmetric(g-3,g-3,g1)
    c: Symmetric(g-4,g-4,g1)
FEATURE [PartDesign::Plane] DatumPlane006
  AttachmentOffset = pos=(0,0,4) rot=(0,0,1;0rad)
  Length = 72.415
  MapMode = 7
  Placement = pos=(30.5,41.1039,73.7355) rot=(1,0,0;2.35076rad)
  ResizeMode = 0
  Support = -> [Sketch017]
  Width = 138.494
FEATURE [Sketcher::SketchObject] Sketch018
  FullyConstrained = true
  MapMode = 5
  Placement = pos=(30.5,41.1039,73.7355) rot=(1,0,0;2.35076rad)
  Support = -> [DatumPlane006]
  sketch-geometry (1):
    g0: Circle CenterX=0 CenterY=0 CenterZ=0 NormalX=0 NormalY=0 NormalZ=1 AngleXU=0 Radius=0.4
  constraints (2):
    c: Diameter(g0) = 0.8
    c: Coincident(g0,g-1)
FEATURE [PartDesign::AdditivePipe] AdditivePipe
  AuxilleryCurvelinear = true
  AuxillerySpineTangent = false
  Binormal = (0,0,0)
  Mode = 0
  Placement = pos=(30.5,41.1039,73.7355) rot=(1,0,0;2.35076rad)
  Profile = -> Sketch018
  Spine = -> Sketch017 [Edge1,Edge2,Edge3,Edge4,Edge5,Edge6,Edge7,Edge8,Edge9]
  SpineTangent = false
  Transformation = 0
  Transition = 0
FEATURE [PartDesign::Body] Body030  label="brass_wire_left"
  Group = -> [Binder028,Binder029,Sketch016,DatumPlane005,Sketch017,DatumPlane006,Sketch018,AdditivePipe]
  Origin = -> Origin033
  Tip = -> AdditivePipe
FEATURE [PartDesign::FeatureBase] Clone013
  BaseFeature = -> Body030
FEATURE [PartDesign::Body] Body031  label="brass_wire_right"
  Group = -> [Clone013]
  Origin = -> Origin034
  Placement = pos=(-4e-15,-32.75,11.6) rot=(0,0.694658,0.71934;3.14159rad)
  Tip = -> Clone013
FEATURE [App::DocumentObjectGroup] Group003  label="other_parts"
  Group = -> [Part001,batt_9V005_cp_sp,Body025,Body026,Body027,Body028,Body029,Body030,Body031]
FEATURE [TechDraw::DrawSVGTemplate] Template
  Height = 210
  Orientation = 1
  Template = <userpath>/Documents/FreeCAD/Templates/A4_Landscape_blank.svg
  Width = 297
FEATURE [TechDraw::DrawViewPart] View
  CoarseView = false
  Direction = (0,-0.707107,0.707107)
  Focus = 100
  HardHidden = false
  IsoCount = 0
  IsoHidden = false
  IsoVisible = false
  LockPosition = false
  Perspective = false
  Rotation = 0
  ScaleType = 0
  ScrubCount = 0
  SeamHidden = false
  SeamVisible = false
  SmoothHidden = false
  SmoothVisible = true
  Source = -> [Body030]
  X = 148.5
  XDirection = (0,0.707107,0.707107)
  Y = 105
FEATURE [TechDraw::DrawViewDimension] Dimension001
  AngleOverride = false
  Arbitrary = false
  ArbitraryTolerances = false
  EqualTolerance = true
  ExtensionAngle = 0
  FormatSpec = %.2w
  FormatSpecOverTolerance = %+.2w
  FormatSpecUnderTolerance = %+.2w
  Inverted = false
  LineAngle = 0
  LockPosition = false
  MeasureType = 1
  OverTolerance = 0
  References2D = -> [View]
  Rotation = 0
  ScaleType = 0
  TheoreticalExact = false
  Type = 1
  UnderTolerance = 0
  X = -15.7775
  Y = 11.3138
FEATURE [TechDraw::DrawViewDimension] Dimension002
  AngleOverride = false
  Arbitrary = false
  ArbitraryTolerances = false
  EqualTolerance = true
  ExtensionAngle = 0
  FormatSpec = %.2w
  FormatSpecOverTolerance = %+.2w
  FormatSpecUnderTolerance = %+.2w
  Inverted = false
  LineAngle = 0
  LockPosition = false
  MeasureType = 1
  OverTolerance = 0
  References2D = -> [View]
  Rotation = 0
  ScaleType = 0
  TheoreticalExact = false
  Type = 2
  UnderTolerance = 0
  X = -41.2836
  Y = 11.8169
FEATURE [TechDraw::DrawViewDimension] Dimension
  AngleOverride = false
  Arbitrary = false
  ArbitraryTolerances = false
  EqualTolerance = true
  ExtensionAngle = 0
  FormatSpec = %.2w
  FormatSpecOverTolerance = %+.2w
  FormatSpecUnderTolerance = %+.2w
  Inverted = false
  LineAngle = 0
  LockPosition = false
  MeasureType = 1
  OverTolerance = 0
  References2D = -> [View]
  Rotation = 0
  ScaleType = 0
  TheoreticalExact = false
  Type = 2
  UnderTolerance = 0
  X = 36.672
  Y = 8.64568
FEATURE [TechDraw::DrawViewDimension] Dimension003
  AngleOverride = false
  Arbitrary = false
  ArbitraryTolerances = false
  EqualTolerance = true
  ExtensionAngle = 0
  FormatSpec = %.2w
  FormatSpecOverTolerance = %+.2w
  FormatSpecUnderTolerance = %+.2w
  Inverted = false
  LineAngle = 0
  LockPosition = false
  MeasureType = 1
  OverTolerance = 0
  References2D = -> [View]
  Rotation = 0
  ScaleType = 0
  TheoreticalExact = false
  Type = 1
  UnderTolerance = 0
  X = 15.7775
  Y = -14.8137
FEATURE [TechDraw::DrawViewDimension] Dimension004
  AngleOverride = false
  Arbitrary = false
  ArbitraryTolerances = false
  EqualTolerance = true
  ExtensionAngle = 0
  FormatSpec = %.2w
  FormatSpecOverTolerance = %+.2w
  FormatSpecUnderTolerance = %+.2w
  Inverted = false
  LineAngle = 0
  LockPosition = false
  MeasureType = 1
  OverTolerance = 0
  References2D = -> [View]
  Rotation = 0
  ScaleType = 0
  TheoreticalExact = false
  Type = 1
  UnderTolerance = 0
  X = 1.18251
  Y = -21.3199
FEATURE [TechDraw::DrawViewAnnotation] Annotation
  Font = Droid Sans Mono
  LineSpace = 100
  LockPosition = false
  MaxWidth = -1
  Rotation = 0
  ScaleType = 0
  Text = Brass Wire, 0.8mm dia | length  = 4+4+2.8+2.8+51.95 | length = approx 66 mm long
  TextSize = 3
  TextStyle = 0
  X = 150.297
  Y = 144.338
FEATURE [TechDraw::DrawPage] Page
  KeepUpdated = true
  NextBalloonIndex = 1
  ProjectionType = 1
  Template = -> Template
  Views = -> [View,Dimension001,Dimension002,Dimension,Dimension003,Dimension004,Annotation]
FEATURE [Sketcher::SketchObject] Sketch019
  FullyConstrained = true
  MapMode = 5
  Placement = pos=(-27.1,7.1e-15,-1.82e-14) rot=(0.57735,-0.57735,-0.57735;2.0944rad)
  Support = -> [Fillet001]
  sketch-geometry (1):
    g0: Circle CenterX=0 CenterY=0 CenterZ=0 NormalX=0 NormalY=0 NormalZ=1 AngleXU=0 Radius=3.5
  constraints (2):
    c: Coincident(g0,g-1)
    c: Diameter(g0) = 7
FEATURE [PartDesign::Pocket] Pocket
  BaseFeature = -> Fillet001
  Direction = (1,-1e-16,5e-16)
  Length = 5
  Length2 = 5
  Placement = pos=(-24.3,8e-15,-1.4e-14) rot=(0.57735,-0.57735,-0.57735;2.0944rad)
  Profile = -> Sketch019
  ReferenceAxis = -> Sketch019 [N_Axis]
  Type = 1
FEATURE [PartDesign::Body] Body002  label="leg_right"
  Group = -> [Sketch001,Binder001,Binder004,DatumPlane003,Pad004,Fillet,Fillet001,Sketch019,Pocket]
  Origin = -> Origin003
  Tip = -> Pocket
FEATURE [PartDesign::FeatureBase] Clone006
  BaseFeature = -> Body002
FEATURE [PartDesign::Body] Body014  label="leg_left"
  Group = -> [Clone006]
  Origin = -> Origin016
  Placement = pos=(0,0,20) rot=(0,0,1;3.14159rad)
  Tip = -> Clone006
FEATURE [App::DocumentObjectGroup] Group002  label="Acrylic_parts"
  Group = -> [Body,Body003,Body004,Body002,Body008,Body009,Body010,Body014,Body007,Body015,Body017,Body018,Body023,Body024,Body022]
FEATURE [Part::Part2DObjectPython] Shape2DView007  label="leg_right_DXF"  # Draft 2D object (typed FeaturePython)
  AutoUpdate = true
  Base = -> Body002
  Clip = false
  FuseArch = false
  HiddenLines = false
  InPlace = true
  OnlySolids = false
  Projection = (-1,0,0)
  ProjectionMode = 0
  SegmentLength = 0.05
  Tessellation = false
  VisibleOnly = false
FEATURE [Part::Part2DObjectPython] Shape2DView011  label="leg_left_DXF"  # Draft 2D object (typed FeaturePython)
  AutoUpdate = true
  Base = -> Body014
  Clip = false
  FuseArch = false
  HiddenLines = false
  InPlace = true
  OnlySolids = false
  Projection = (1,0,0)
  ProjectionMode = 0
  SegmentLength = 0.05
  Tessellation = false
  VisibleOnly = false
FEATURE [App::DocumentObjectGroup] Group004  label="DXF_acrylic"
  Group = -> [Shape2DView,Shape2DView001,Shape2DView002,Shape2DView003,Shape2DView004,Shape2DView005,Shape2DView006,Shape2DView007,Shape2DView008,Shape2DView009,Shape2DView010,Shape2DView011,Shape2DView012,Shape2DView013,Shape2DView014,Shape2DView015,Shape2DView016,Shape2DView018,Shape2DView019]
